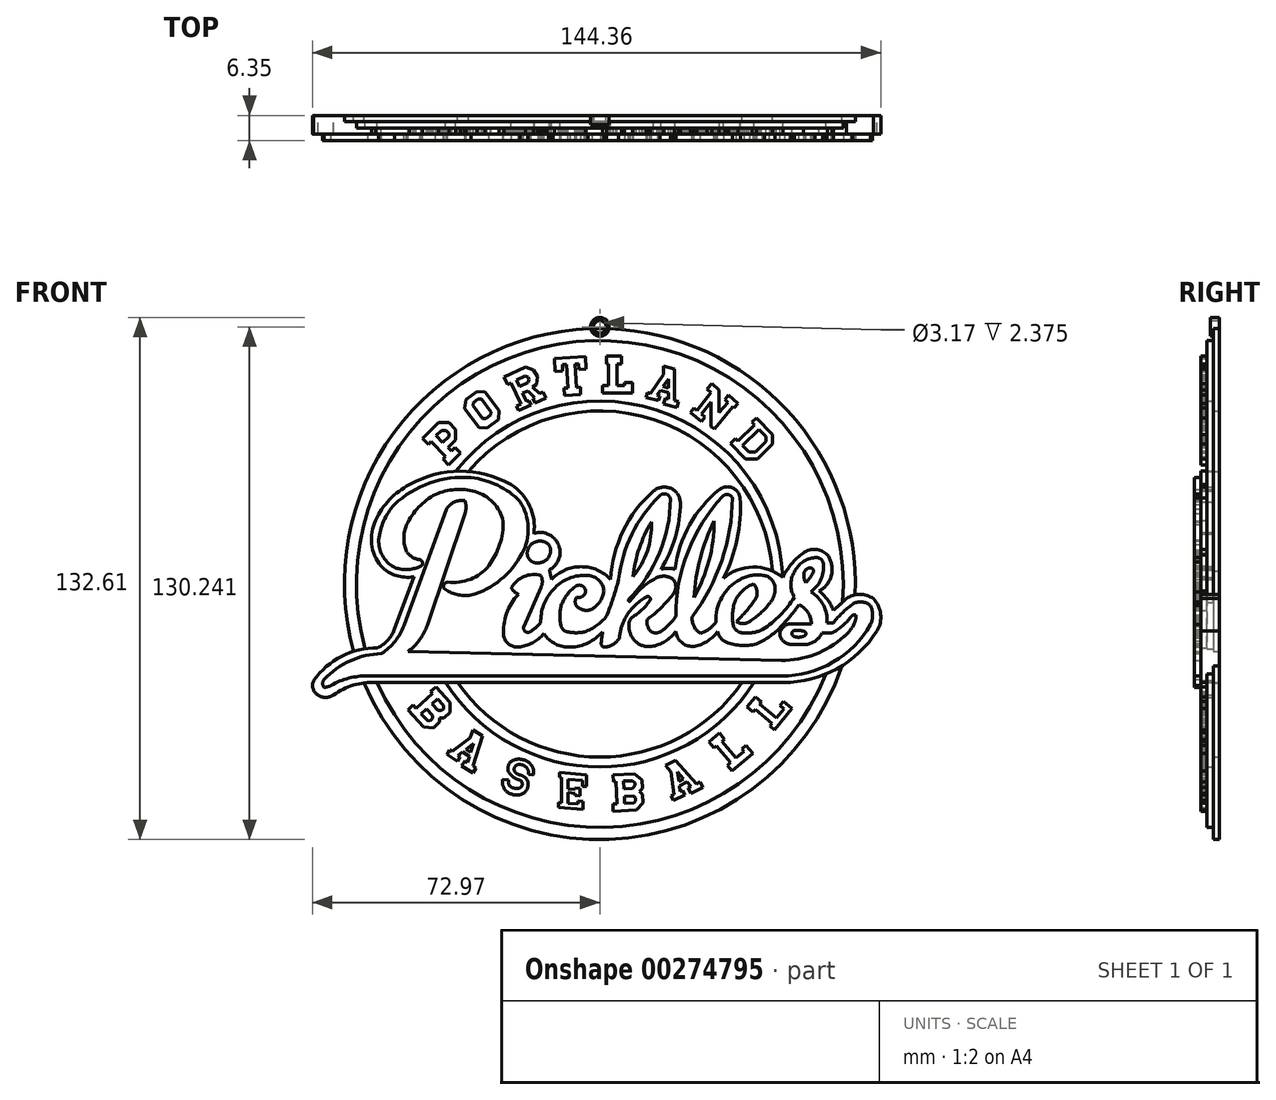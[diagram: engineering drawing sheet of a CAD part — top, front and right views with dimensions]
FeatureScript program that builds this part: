
annotation { "Feature Type Name" : "Feature", "Feature Type Description" : "" }
export const myFeature = defineFeature(function(context is Context, id is Id, definition is map)
    precondition{}
    {
        {
            var Q0;
            Q0=qCreatedBy(makeId("Front.planeOp"),FACE);
            var sketch = newSketch(context, id + "F0", { "sketchPlane" : qUnion([Q0])});
            skCircle(sketch, "E0", {"center": v(0, 0) * mm, "radius": 64.91 * mm});
            skCircle(sketch, "E1", {"center": v(0, 0) * mm, "radius": 43.97 * mm});
            skSolve(sketch);
        }
        {
            var Q0;
            Q0=makeQuery(id+"F0.imprint","IMPRINT",FACE,{"disambiguationData":[TD([[makeQuery(id+"F0.imprint","IMPRINT",EDGE,{"derivedFrom":sQuery(id+"F0.wireOp",EDGE,"E0")}),1.0]])]});
            extrude(context, id + "F1", {"entities" : qUnion([Q0]), "depth" : 1.59 * mm});
        }
        {
            var Q0;
            Q0=makeQuery(id+"F1.opExtrude","CAP_FACE",FACE,{"disambiguationData":[OSD([sQuery(id+"F0.wireOp",EDGE,"E0"),sQuery(id+"F0.wireOp",EDGE,"E1")])],"isStart":false});
            var sketch = newSketch(context, id + "F2", { "sketchPlane" : qUnion([Q0])});
            skCircle(sketch, "E2", {"center": v(0, 0) * mm, "radius": 61.84 * mm});
            skCircle(sketch, "E3", {"center": v(0, 0) * mm, "radius": 46.5 * mm});
            skSolve(sketch);
        }
        {
            var Q0;
            Q0=makeQuery(id+"F2.imprint","IMPRINT",FACE,{"disambiguationData":[TD([[makeQuery(id+"F2.imprint","IMPRINT",EDGE,{"derivedFrom":sQuery(id+"F2.wireOp",EDGE,"E2")}),1.0]])]});
            extrude(context, id + "F3", {"entities" : qUnion([Q0]), "operationType" : NewBodyOperationType.ADD, "depth" : 1.59 * mm});
        }
        {
            var Q0;
            Q0=makeQuery(id+"F3.opExtrude","CAP_FACE",FACE,{"disambiguationData":[OSD([sQuery(id+"F2.wireOp",EDGE,"E2"),sQuery(id+"F2.wireOp",EDGE,"E3")])],"isStart":false});
            var sketch = newSketch(context, id + "F4", { "sketchPlane" : qUnion([Q0])});
            skLineSegment(sketch, "E4", {"start": v(-45, 37.01) * mm, "end": v(-43.54, 35.5) * mm});
            skLineSegment(sketch, "E5", {"start": v(-43.54, 35.5) * mm, "end": v(-42.88, 36.15) * mm});
            skLineSegment(sketch, "E6", {"start": v(-42.88, 36.15) * mm, "end": v(-39.2, 32.36) * mm});
            skLineSegment(sketch, "E7", {"start": v(-39.2, 32.36) * mm, "end": v(-39.83, 31.75) * mm});
            skLineSegment(sketch, "E8", {"start": v(-39.83, 31.75) * mm, "end": v(-38.41, 30.3) * mm});
            skLineSegment(sketch, "E9", {"start": v(-38.41, 30.3) * mm, "end": v(-35.38, 33.24) * mm});
            skLineSegment(sketch, "E10", {"start": v(-35.38, 33.24) * mm, "end": v(-36.8, 34.7) * mm});
            skLineSegment(sketch, "E11", {"start": v(-36.8, 34.7) * mm, "end": v(-37.7, 33.84) * mm});
            skLineSegment(sketch, "E12", {"start": v(-37.7, 33.84) * mm, "end": v(-38.57, 34.73) * mm});
            skLineSegment(sketch, "E13", {"start": v(-38.57, 34.73) * mm, "end": v(-36.65, 36.6) * mm});
            skLineSegment(sketch, "E14", {"start": v(-36.65, 36.6) * mm, "end": v(-36.65, 39.24) * mm});
            skLineSegment(sketch, "E15", {"start": v(-36.65, 39.24) * mm, "end": v(-38.37, 41.02) * mm});
            skLineSegment(sketch, "E16", {"start": v(-45, 37.01) * mm, "end": v(-40.92, 40.98) * mm});
            skLineSegment(sketch, "E17", {"start": v(-40.92, 40.98) * mm, "end": v(-38.37, 41.02) * mm});
            skLineSegment(sketch, "E18", {"start": v(-41.62, 37.68) * mm, "end": v(-40.2, 39.06) * mm});
            skLineSegment(sketch, "E19", {"start": v(-40.2, 39.06) * mm, "end": v(-39.12, 39.06) * mm});
            skLineSegment(sketch, "E20", {"start": v(-39.12, 39.06) * mm, "end": v(-38.37, 38.29) * mm});
            skLineSegment(sketch, "E21", {"start": v(-38.37, 38.29) * mm, "end": v(-38.37, 37.5) * mm});
            skLineSegment(sketch, "E22", {"start": v(-41.62, 37.68) * mm, "end": v(-39.95, 35.96) * mm});
            skLineSegment(sketch, "E23", {"start": v(-38.37, 37.5) * mm, "end": v(-39.95, 35.96) * mm});
            skLineSegment(sketch, "E24", {"start": v(-33.96, 46.9) * mm, "end": v(-31.25, 48.95) * mm});
            skLineSegment(sketch, "E25", {"start": v(-31.25, 48.95) * mm, "end": v(-29.18, 48.82) * mm});
            skLineSegment(sketch, "E26", {"start": v(-29.18, 48.82) * mm, "end": v(-25.57, 44.04) * mm});
            skLineSegment(sketch, "E27", {"start": v(-25.57, 44.04) * mm, "end": v(-25.7, 41.85) * mm});
            skLineSegment(sketch, "E28", {"start": v(-25.7, 41.85) * mm, "end": v(-28.67, 39.6) * mm});
            skLineSegment(sketch, "E29", {"start": v(-28.67, 39.6) * mm, "end": v(-30.7, 39.74) * mm});
            skLineSegment(sketch, "E30", {"start": v(-30.7, 39.74) * mm, "end": v(-34.33, 44.53) * mm});
            skLineSegment(sketch, "E31", {"start": v(-34.33, 44.53) * mm, "end": v(-33.96, 46.9) * mm});
            skLineSegment(sketch, "E32", {"start": v(-32.06, 46.14) * mm, "end": v(-30.93, 47) * mm});
            skLineSegment(sketch, "E33", {"start": v(-30.07, 46.95) * mm, "end": v(-27.63, 43.73) * mm});
            skLineSegment(sketch, "E34", {"start": v(-27.8, 42.88) * mm, "end": v(-28.94, 42.02) * mm});
            skLineSegment(sketch, "E35", {"start": v(-29.8, 42.09) * mm, "end": v(-32.24, 45.3) * mm});
            skLineSegment(sketch, "E36", {"start": v(-24.28, 52.53) * mm, "end": v(-18.82, 55.07) * mm});
            skLineSegment(sketch, "E37", {"start": v(-18.82, 55.07) * mm, "end": v(-16.83, 54.38) * mm});
            skLineSegment(sketch, "E38", {"start": v(-16.83, 54.38) * mm, "end": v(-15.86, 52.67) * mm});
            skLineSegment(sketch, "E39", {"start": v(-15.86, 52.67) * mm, "end": v(-16.12, 50.74) * mm});
            skLineSegment(sketch, "E40", {"start": v(-16.12, 50.74) * mm, "end": v(-17.06, 50.05) * mm});
            skLineSegment(sketch, "E41", {"start": v(-17.06, 50.05) * mm, "end": v(-15.38, 48.37) * mm});
            skLineSegment(sketch, "E42", {"start": v(-15.38, 48.37) * mm, "end": v(-14.38, 48.84) * mm});
            skLineSegment(sketch, "E43", {"start": v(-14.38, 48.84) * mm, "end": v(-13.66, 47.27) * mm});
            skLineSegment(sketch, "E44", {"start": v(-13.66, 47.27) * mm, "end": v(-16.45, 45.97) * mm});
            skLineSegment(sketch, "E45", {"start": v(-16.45, 45.97) * mm, "end": v(-16.98, 47.12) * mm});
            skLineSegment(sketch, "E46", {"start": v(-16.98, 47.12) * mm, "end": v(-16.56, 47.32) * mm});
            skLineSegment(sketch, "E47", {"start": v(-16.56, 47.32) * mm, "end": v(-18.3, 49.06) * mm});
            skLineSegment(sketch, "E48", {"start": v(-18.3, 49.06) * mm, "end": v(-19.58, 48.47) * mm});
            skLineSegment(sketch, "E49", {"start": v(-19.58, 48.47) * mm, "end": v(-18.7, 46.55) * mm});
            skPoint(sketch, "E49.endSnap0", {"position": v(-16.72, 46.55) * mm});
            skLineSegment(sketch, "E50", {"start": v(-17.96, 46.67) * mm, "end": v(-18.6, 46.37) * mm});
            skLineSegment(sketch, "E51", {"start": v(-18.7, 46.55) * mm, "end": v(-18.6, 46.37) * mm});
            skLineSegment(sketch, "E52", {"start": v(-17.96, 46.67) * mm, "end": v(-17.42, 45.52) * mm});
            skLineSegment(sketch, "E53", {"start": v(-17.42, 45.52) * mm, "end": v(-20.63, 44.03) * mm});
            skPoint(sketch, "E54.orphan", {"position": v(-18.93, 46.22) * mm});
            skLineSegment(sketch, "E55", {"start": v(-20.63, 44.03) * mm, "end": v(-21.17, 45.18) * mm});
            skLineSegment(sketch, "E56", {"start": v(-20.07, 45.69) * mm, "end": v(-22.6, 51.12) * mm});
            skLineSegment(sketch, "E57", {"start": v(-22.6, 51.12) * mm, "end": v(-23.45, 50.73) * mm});
            skLineSegment(sketch, "E58.trimOffspring", {"start": v(-20.07, 45.69) * mm, "end": v(-21.17, 45.18) * mm});
            skLineSegment(sketch, "E59", {"start": v(-24.28, 52.53) * mm, "end": v(-23.45, 50.73) * mm});
            skLineSegment(sketch, "E60", {"start": v(-21.14, 51.8) * mm, "end": v(-19, 52.8) * mm});
            skLineSegment(sketch, "E61", {"start": v(-18.2, 52.53) * mm, "end": v(-17.94, 51.95) * mm});
            skLineSegment(sketch, "E62", {"start": v(-18.25, 51.17) * mm, "end": v(-20.38, 50.18) * mm});
            skPoint(sketch, "E63.trimOffspring.end.orphan", {"position": v(-22.6, 54.96) * mm});
            skPoint(sketch, "E64.orphan", {"position": v(-14.3, 54.99) * mm});
            skLineSegment(sketch, "E65", {"start": v(-20.38, 50.18) * mm, "end": v(-21.14, 51.8) * mm});
            skLineSegment(sketch, "E66", {"start": v(-19, 52.8) * mm, "end": v(-18.2, 52.53) * mm});
            skLineSegment(sketch, "E67", {"start": v(-18.25, 51.17) * mm, "end": v(-17.94, 51.95) * mm});
            skPoint(sketch, "E68.orphan", {"position": v(-17.7, 49.97) * mm});
            skPoint(sketch, "E69.orphan", {"position": v(-18.45, 53.06) * mm});
            skPoint(sketch, "E70.orphan", {"position": v(-17.7, 51.43) * mm});
            skLineSegment(sketch, "E71", {"start": v(-30.07, 46.95) * mm, "end": v(-30.93, 47) * mm});
            skPoint(sketch, "E72.trimOffspring.end.orphan", {"position": v(-29.43, 44.98) * mm});
            skPoint(sketch, "E73.orphan", {"position": v(-29.3, 46.9) * mm});
            skLineSegment(sketch, "E74", {"start": v(-32.24, 45.3) * mm, "end": v(-32.06, 46.14) * mm});
            skLineSegment(sketch, "E75", {"start": v(-28.94, 42.02) * mm, "end": v(-29.8, 42.09) * mm});
            skLineSegment(sketch, "E76", {"start": v(-27.8, 42.88) * mm, "end": v(-27.63, 43.73) * mm});
            skLineSegment(sketch, "E77", {"start": v(-4.17, 57.71) * mm, "end": v(-11.54, 57.23) * mm});
            skLineSegment(sketch, "E78", {"start": v(-11.54, 57.23) * mm, "end": v(-11.33, 54.04) * mm});
            skLineSegment(sketch, "E79", {"start": v(-9.42, 54.17) * mm, "end": v(-9.47, 54.9) * mm});
            skLineSegment(sketch, "E80", {"start": v(-8.4, 54.96) * mm, "end": v(-8.06, 49.81) * mm});
            skLineSegment(sketch, "E81", {"start": v(-8.06, 49.81) * mm, "end": v(-9.05, 49.75) * mm});
            skLineSegment(sketch, "E82", {"start": v(-9.05, 49.75) * mm, "end": v(-8.93, 47.87) * mm});
            skLineSegment(sketch, "E83", {"start": v(-8.93, 47.87) * mm, "end": v(-4.85, 48.14) * mm});
            skLineSegment(sketch, "E84", {"start": v(-6.32, 55.1) * mm, "end": v(-5.98, 49.97) * mm});
            skPoint(sketch, "E84.endSnap0", {"position": v(-5.64, 49.97) * mm});
            skLineSegment(sketch, "E85", {"start": v(-4.85, 48.14) * mm, "end": v(-4.97, 50.02) * mm});
            skLineSegment(sketch, "E86", {"start": v(-4.17, 57.71) * mm, "end": v(-3.7, 57.74) * mm});
            skLineSegment(sketch, "E87", {"start": v(-3.7, 57.74) * mm, "end": v(-3.5, 54.56) * mm});
            skLineSegment(sketch, "E88.trimOffspring", {"start": v(-5.26, 54.44) * mm, "end": v(-5.31, 55.17) * mm});
            skPoint(sketch, "E89.orphan", {"position": v(-3.22, 50.13) * mm});
            skLineSegment(sketch, "E90", {"start": v(-4.97, 50.02) * mm, "end": v(-5.98, 49.95) * mm});
            skLineSegment(sketch, "E91", {"start": v(-5.98, 49.97) * mm, "end": v(-5.98, 49.95) * mm});
            skLineSegment(sketch, "E92", {"start": v(-9.47, 54.9) * mm, "end": v(-9.52, 55.7) * mm});
            skLineSegment(sketch, "E93", {"start": v(-8.4, 54.96) * mm, "end": v(-8.46, 55.77) * mm});
            skLineSegment(sketch, "E94", {"start": v(-6.32, 55.1) * mm, "end": v(-6.37, 55.9) * mm});
            skLineSegment(sketch, "E95", {"start": v(-5.31, 55.17) * mm, "end": v(-5.36, 55.98) * mm});
            skLineSegment(sketch, "E96", {"start": v(-9.52, 55.7) * mm, "end": v(-8.46, 55.77) * mm});
            skLineSegment(sketch, "E97.trimOffspring", {"start": v(-6.37, 55.9) * mm, "end": v(-5.36, 55.98) * mm});
            skLineSegment(sketch, "E98", {"start": v(-5.26, 54.44) * mm, "end": v(-3.5, 54.56) * mm});
            skLineSegment(sketch, "E99", {"start": v(-9.42, 54.17) * mm, "end": v(-11.33, 54.04) * mm});
            skPoint(sketch, "E100.orphan", {"position": v(-5.22, 53.71) * mm});
            skLineSegment(sketch, "E101", {"start": v(1.68, 57.94) * mm, "end": v(5.56, 57.94) * mm});
            skLineSegment(sketch, "E102", {"start": v(5.56, 57.94) * mm, "end": v(5.56, 55.91) * mm});
            skLineSegment(sketch, "E103", {"start": v(5.56, 55.91) * mm, "end": v(4.33, 55.91) * mm});
            skLineSegment(sketch, "E104", {"start": v(4.33, 55.91) * mm, "end": v(4.33, 50.37) * mm});
            skLineSegment(sketch, "E105", {"start": v(4.33, 50.37) * mm, "end": v(6.25, 50.37) * mm});
            skLineSegment(sketch, "E106", {"start": v(6.25, 50.37) * mm, "end": v(6.25, 51.2) * mm});
            skLineSegment(sketch, "E107", {"start": v(6.25, 51.2) * mm, "end": v(8.32, 51.2) * mm});
            skLineSegment(sketch, "E108", {"start": v(8.32, 51.2) * mm, "end": v(8.32, 48.49) * mm});
            skLineSegment(sketch, "E109", {"start": v(8.32, 48.49) * mm, "end": v(0.63, 48.49) * mm});
            skLineSegment(sketch, "E110", {"start": v(0.63, 48.49) * mm, "end": v(0.63, 50.37) * mm});
            skLineSegment(sketch, "E111", {"start": v(0.63, 50.37) * mm, "end": v(2.18, 50.37) * mm});
            skLineSegment(sketch, "E112", {"start": v(2.18, 50.37) * mm, "end": v(2.18, 55.91) * mm});
            skLineSegment(sketch, "E113", {"start": v(2.18, 55.91) * mm, "end": v(1.68, 55.91) * mm});
            skLineSegment(sketch, "E114", {"start": v(1.68, 55.91) * mm, "end": v(1.68, 57.94) * mm});
            skPoint(sketch, "E115.endSnap0", {"position": v(16.46, 48.8) * mm});
            skLineSegment(sketch, "E116", {"start": v(16.22, 45.8) * mm, "end": v(19.55, 44.89) * mm});
            skLineSegment(sketch, "E117", {"start": v(19.95, 46.35) * mm, "end": v(19, 46.61) * mm});
            skLineSegment(sketch, "E118", {"start": v(19, 46.61) * mm, "end": v(19, 54.59) * mm});
            skLineSegment(sketch, "E119", {"start": v(16.14, 53.17) * mm, "end": v(13.1, 48.82) * mm});
            skLineSegment(sketch, "E120", {"start": v(17.44, 47.04) * mm, "end": v(16.62, 47.26) * mm});
            skLineSegment(sketch, "E121", {"start": v(16.22, 45.8) * mm, "end": v(16.62, 47.26) * mm});
            skLineSegment(sketch, "E122", {"start": v(11.77, 47.41) * mm, "end": v(14.88, 46.57) * mm});
            skLineSegment(sketch, "E123", {"start": v(14.88, 46.57) * mm, "end": v(15.22, 47.8) * mm});
            skLineSegment(sketch, "E124", {"start": v(15.22, 47.8) * mm, "end": v(14.57, 47.99) * mm});
            skLineSegment(sketch, "E125", {"start": v(13.1, 48.82) * mm, "end": v(12.85, 48.45) * mm});
            skLineSegment(sketch, "E126", {"start": v(14.57, 47.99) * mm, "end": v(15.2, 48.9) * mm});
            skLineSegment(sketch, "E127", {"start": v(17.44, 48.44) * mm, "end": v(17.44, 47.04) * mm});
            skLineSegment(sketch, "E128", {"start": v(15.51, 49.13) * mm, "end": v(17.44, 48.6) * mm});
            skLineSegment(sketch, "E129", {"start": v(17.44, 48.6) * mm, "end": v(17.44, 48.44) * mm});
            skLineSegment(sketch, "E130", {"start": v(15.2, 48.9) * mm, "end": v(15.4, 49.16) * mm});
            skLineSegment(sketch, "E131", {"start": v(15.51, 49.13) * mm, "end": v(15.4, 49.16) * mm});
            skLineSegment(sketch, "E132", {"start": v(19, 54.59) * mm, "end": v(16.18, 55.35) * mm});
            skLineSegment(sketch, "E133", {"start": v(16.18, 55.35) * mm, "end": v(16.14, 53.17) * mm});
            skLineSegment(sketch, "E134", {"start": v(16.07, 50.12) * mm, "end": v(17.4, 49.76) * mm});
            skLineSegment(sketch, "E135", {"start": v(17.4, 49.76) * mm, "end": v(17.4, 52.14) * mm});
            skLineSegment(sketch, "E136", {"start": v(17.4, 52.14) * mm, "end": v(16.07, 50.12) * mm});
            skLineSegment(sketch, "E137.trimOffspring", {"start": v(12.85, 48.45) * mm, "end": v(12.1, 48.66) * mm});
            skLineSegment(sketch, "E138", {"start": v(12.1, 48.66) * mm, "end": v(11.77, 47.41) * mm});
            skLineSegment(sketch, "E139", {"start": v(19.95, 46.35) * mm, "end": v(19.55, 44.89) * mm});
            skLineSegment(sketch, "E140", {"start": v(28.44, 50.95) * mm, "end": v(30.3, 49.32) * mm});
            skLineSegment(sketch, "E141", {"start": v(30.3, 49.32) * mm, "end": v(30.3, 43.62) * mm});
            skLineSegment(sketch, "E142", {"start": v(32.75, 47.97) * mm, "end": v(35.12, 45.9) * mm});
            skLineSegment(sketch, "E143", {"start": v(35.12, 45.9) * mm, "end": v(34.32, 44.97) * mm});
            skLineSegment(sketch, "E144", {"start": v(33.77, 45.07) * mm, "end": v(29.11, 39.33) * mm});
            skLineSegment(sketch, "E145", {"start": v(28.29, 40) * mm, "end": v(28.29, 46.3) * mm});
            skLineSegment(sketch, "E146", {"start": v(28.29, 46.3) * mm, "end": v(26.06, 43.55) * mm});
            skLineSegment(sketch, "E147", {"start": v(26.06, 43.55) * mm, "end": v(25.77, 43.2) * mm});
            skLineSegment(sketch, "E148", {"start": v(25.77, 43.2) * mm, "end": v(26.67, 42.46) * mm});
            skLineSegment(sketch, "E149", {"start": v(25.76, 41.33) * mm, "end": v(23.01, 43.56) * mm});
            skLineSegment(sketch, "E150", {"start": v(26.67, 42.46) * mm, "end": v(25.76, 41.33) * mm});
            skLineSegment(sketch, "E151", {"start": v(32.75, 47.97) * mm, "end": v(31.94, 47.04) * mm});
            skLineSegment(sketch, "E152", {"start": v(31.76, 46.83) * mm, "end": v(32.53, 46.16) * mm});
            skLineSegment(sketch, "E153", {"start": v(31.94, 47.04) * mm, "end": v(31.76, 46.83) * mm});
            skLineSegment(sketch, "E154", {"start": v(34.32, 44.97) * mm, "end": v(34.13, 44.76) * mm});
            skLineSegment(sketch, "E155", {"start": v(30.3, 43.62) * mm, "end": v(32.53, 46.16) * mm});
            skLineSegment(sketch, "E156.trimOffspring", {"start": v(33.77, 45.07) * mm, "end": v(34.13, 44.76) * mm});
            skLineSegment(sketch, "E157", {"start": v(28.44, 50.95) * mm, "end": v(27.27, 49.5) * mm});
            skLineSegment(sketch, "E158", {"start": v(24.62, 44.13) * mm, "end": v(23.93, 44.7) * mm});
            skLineSegment(sketch, "E159", {"start": v(23.01, 43.56) * mm, "end": v(23.93, 44.7) * mm});
            skLineSegment(sketch, "E160", {"start": v(24.62, 44.13) * mm, "end": v(27.98, 48.26) * mm});
            skLineSegment(sketch, "E161", {"start": v(27.98, 48.26) * mm, "end": v(28.3, 48.66) * mm});
            skLineSegment(sketch, "E162", {"start": v(28.3, 48.66) * mm, "end": v(27.27, 49.5) * mm});
            skPoint(sketch, "E163.orphan", {"position": v(27.81, 39.67) * mm});
            skLineSegment(sketch, "E164", {"start": v(28.29, 40) * mm, "end": v(29.11, 39.33) * mm});
            skPoint(sketch, "E165.orphan", {"position": v(28.29, 39.29) * mm});
            skPoint(sketch, "E166.orphan", {"position": v(29.17, 39.29) * mm});
            skPoint(sketch, "E167.orphan", {"position": v(28.76, 38.9) * mm});
            skLineSegment(sketch, "E168", {"start": v(39.8, 42.2) * mm, "end": v(43.91, 38) * mm});
            skPoint(sketch, "E168.startSnap0", {"position": v(31.44, 42.2) * mm});
            skLineSegment(sketch, "E169", {"start": v(43.91, 38) * mm, "end": v(43.92, 35.6) * mm});
            skLineSegment(sketch, "E170", {"start": v(43.92, 35.6) * mm, "end": v(40.1, 31.82) * mm});
            skLineSegment(sketch, "E171", {"start": v(40.1, 31.82) * mm, "end": v(36.96, 31.82) * mm});
            skLineSegment(sketch, "E172", {"start": v(36.96, 31.82) * mm, "end": v(33.16, 35.7) * mm});
            skLineSegment(sketch, "E173", {"start": v(39.8, 42.2) * mm, "end": v(38.67, 41.1) * mm});
            skLineSegment(sketch, "E174", {"start": v(38.67, 41.1) * mm, "end": v(39.3, 40.46) * mm});
            skLineSegment(sketch, "E175", {"start": v(39.3, 40.46) * mm, "end": v(35.08, 36.33) * mm});
            skLineSegment(sketch, "E176", {"start": v(35.08, 36.33) * mm, "end": v(34.45, 36.97) * mm});
            skLineSegment(sketch, "E177", {"start": v(40.48, 39.26) * mm, "end": v(42.25, 37.44) * mm});
            skLineSegment(sketch, "E178.trimOffspring", {"start": v(34.45, 36.97) * mm, "end": v(33.16, 35.7) * mm});
            skLineSegment(sketch, "E179", {"start": v(42.25, 37.44) * mm, "end": v(42.25, 36.2) * mm});
            skLineSegment(sketch, "E180", {"start": v(42.25, 36.2) * mm, "end": v(39.5, 33.5) * mm});
            skLineSegment(sketch, "E181", {"start": v(39.5, 33.5) * mm, "end": v(37.84, 33.5) * mm});
            skLineSegment(sketch, "E182", {"start": v(40.48, 39.26) * mm, "end": v(36.26, 35.13) * mm});
            skPoint(sketch, "E183.orphan", {"position": v(45.2, 34.43) * mm});
            skLineSegment(sketch, "E184", {"start": v(36.26, 35.13) * mm, "end": v(37.84, 33.5) * mm});
            skLineSegment(sketch, "E185", {"start": v(-48.78, -32.01) * mm, "end": v(-47.4, -30.75) * mm});
            skLineSegment(sketch, "E186", {"start": v(-47.4, -30.75) * mm, "end": v(-46.64, -31.58) * mm});
            skLineSegment(sketch, "E187", {"start": v(-46.64, -31.58) * mm, "end": v(-42.48, -27.78) * mm});
            skLineSegment(sketch, "E188", {"start": v(-42.48, -27.78) * mm, "end": v(-42.96, -27.26) * mm});
            skLineSegment(sketch, "E189", {"start": v(-42.96, -27.26) * mm, "end": v(-41.68, -26.1) * mm});
            skLineSegment(sketch, "E190", {"start": v(-41.68, -26.1) * mm, "end": v(-38, -30.12) * mm});
            skLineSegment(sketch, "E191", {"start": v(-38, -30.12) * mm, "end": v(-38, -32.6) * mm});
            skLineSegment(sketch, "E192", {"start": v(-38, -32.6) * mm, "end": v(-39.56, -34.03) * mm});
            skLineSegment(sketch, "E193", {"start": v(-39.56, -34.03) * mm, "end": v(-40.68, -34.03) * mm});
            skLineSegment(sketch, "E194", {"start": v(-40.68, -34.03) * mm, "end": v(-40.68, -35.05) * mm});
            skLineSegment(sketch, "E195", {"start": v(-40.68, -35.05) * mm, "end": v(-42.3, -36.53) * mm});
            skLineSegment(sketch, "E196", {"start": v(-48.78, -32.01) * mm, "end": v(-44.8, -36.37) * mm});
            skLineSegment(sketch, "E197", {"start": v(-44.8, -36.37) * mm, "end": v(-42.3, -36.53) * mm});
            skLineSegment(sketch, "E198", {"start": v(-45.36, -33) * mm, "end": v(-43.8, -34.7) * mm});
            skLineSegment(sketch, "E199", {"start": v(-43.8, -34.7) * mm, "end": v(-43.1, -34.74) * mm});
            skLineSegment(sketch, "E200", {"start": v(-43.1, -34.74) * mm, "end": v(-42.53, -34.21) * mm});
            skLineSegment(sketch, "E201", {"start": v(-42.53, -34.21) * mm, "end": v(-42.48, -33.45) * mm});
            skLineSegment(sketch, "E202", {"start": v(-42.48, -33.45) * mm, "end": v(-44.02, -31.77) * mm});
            skLineSegment(sketch, "E203", {"start": v(-44.02, -31.77) * mm, "end": v(-45.36, -33) * mm});
            skLineSegment(sketch, "E204", {"start": v(-41.2, -29.2) * mm, "end": v(-39.7, -30.83) * mm});
            skLineSegment(sketch, "E205", {"start": v(-42.64, -30.51) * mm, "end": v(-41.2, -29.2) * mm});
            skLineSegment(sketch, "E206", {"start": v(-40.19, -32.14) * mm, "end": v(-39.7, -31.7) * mm});
            skLineSegment(sketch, "E207", {"start": v(-39.7, -31.7) * mm, "end": v(-39.7, -30.83) * mm});
            skLineSegment(sketch, "E208", {"start": v(-42.64, -30.51) * mm, "end": v(-41.15, -32.14) * mm});
            skLineSegment(sketch, "E209", {"start": v(-41.15, -32.14) * mm, "end": v(-40.19, -32.14) * mm});
            skLineSegment(sketch, "E210", {"start": v(-35.14, -46.17) * mm, "end": v(-32.25, -48.06) * mm});
            skLineSegment(sketch, "E211", {"start": v(-31.42, -46.78) * mm, "end": v(-32.24, -46.25) * mm});
            skLineSegment(sketch, "E212", {"start": v(-32.24, -46.25) * mm, "end": v(-29.78, -38.66) * mm});
            skLineSegment(sketch, "E213", {"start": v(-32.94, -39.12) * mm, "end": v(-37.18, -42.32) * mm});
            skLineSegment(sketch, "E214", {"start": v(-33.6, -45.36) * mm, "end": v(-34.3, -44.9) * mm});
            skLineSegment(sketch, "E215", {"start": v(-35.14, -46.17) * mm, "end": v(-34.3, -44.9) * mm});
            skLineSegment(sketch, "E216", {"start": v(-38.87, -43.25) * mm, "end": v(-36.17, -45.01) * mm});
            skLineSegment(sketch, "E217", {"start": v(-36.17, -45.01) * mm, "end": v(-35.47, -43.94) * mm});
            skLineSegment(sketch, "E218", {"start": v(-35.47, -43.94) * mm, "end": v(-36.03, -43.57) * mm});
            skLineSegment(sketch, "E219", {"start": v(-37.18, -42.32) * mm, "end": v(-37.53, -42.6) * mm});
            skLineSegment(sketch, "E220", {"start": v(-36.03, -43.57) * mm, "end": v(-35.15, -42.9) * mm});
            skLineSegment(sketch, "E221", {"start": v(-33.17, -44.02) * mm, "end": v(-33.6, -45.36) * mm});
            skLineSegment(sketch, "E222", {"start": v(-34.79, -42.77) * mm, "end": v(-33.12, -43.87) * mm});
            skLineSegment(sketch, "E223", {"start": v(-35.15, -42.9) * mm, "end": v(-34.9, -42.7) * mm});
            skLineSegment(sketch, "E224", {"start": v(-34.79, -42.77) * mm, "end": v(-34.9, -42.7) * mm});
            skLineSegment(sketch, "E225", {"start": v(-29.78, -38.66) * mm, "end": v(-32.23, -37.06) * mm});
            skLineSegment(sketch, "E226", {"start": v(-32.23, -37.06) * mm, "end": v(-32.94, -39.12) * mm});
            skLineSegment(sketch, "E227", {"start": v(-33.95, -42) * mm, "end": v(-32.8, -42.76) * mm});
            skLineSegment(sketch, "E228", {"start": v(-32.8, -42.76) * mm, "end": v(-32.05, -40.5) * mm});
            skLineSegment(sketch, "E229", {"start": v(-32.05, -40.5) * mm, "end": v(-33.95, -42) * mm});
            skLineSegment(sketch, "E230.trimOffspring", {"start": v(-37.53, -42.6) * mm, "end": v(-38.17, -42.17) * mm});
            skLineSegment(sketch, "E231", {"start": v(-38.17, -42.17) * mm, "end": v(-38.87, -43.25) * mm});
            skLineSegment(sketch, "E232", {"start": v(-31.42, -46.78) * mm, "end": v(-32.25, -48.06) * mm});
            skLineSegment(sketch, "E233", {"start": v(23.1, -53.2) * mm, "end": v(26.17, -51.65) * mm});
            skLineSegment(sketch, "E234", {"start": v(25.48, -50.3) * mm, "end": v(24.6, -50.73) * mm});
            skLineSegment(sketch, "E235", {"start": v(24.6, -50.73) * mm, "end": v(19.26, -44.82) * mm});
            skLineSegment(sketch, "E236", {"start": v(18.08, -47.79) * mm, "end": v(18.75, -53.06) * mm});
            skLineSegment(sketch, "E237", {"start": v(23.16, -51.47) * mm, "end": v(22.4, -51.85) * mm});
            skLineSegment(sketch, "E238", {"start": v(23.1, -53.2) * mm, "end": v(22.4, -51.85) * mm});
            skLineSegment(sketch, "E239", {"start": v(18.7, -55) * mm, "end": v(21.58, -53.53) * mm});
            skLineSegment(sketch, "E240", {"start": v(21.58, -53.53) * mm, "end": v(21, -52.38) * mm});
            skLineSegment(sketch, "E241", {"start": v(21, -52.38) * mm, "end": v(20.4, -52.69) * mm});
            skLineSegment(sketch, "E242", {"start": v(18.75, -53.06) * mm, "end": v(18.8, -53.5) * mm});
            skLineSegment(sketch, "E243", {"start": v(20.4, -52.69) * mm, "end": v(20.26, -51.6) * mm});
            skLineSegment(sketch, "E244", {"start": v(22.22, -50.43) * mm, "end": v(23.16, -51.47) * mm});
            skLineSegment(sketch, "E245", {"start": v(20.33, -51.21) * mm, "end": v(22.1, -50.3) * mm});
            skLineSegment(sketch, "E246", {"start": v(22.1, -50.3) * mm, "end": v(22.22, -50.43) * mm});
            skLineSegment(sketch, "E247", {"start": v(20.26, -51.6) * mm, "end": v(20.22, -51.27) * mm});
            skLineSegment(sketch, "E248", {"start": v(20.33, -51.21) * mm, "end": v(20.22, -51.27) * mm});
            skLineSegment(sketch, "E249", {"start": v(19.26, -44.82) * mm, "end": v(16.65, -46.14) * mm});
            skLineSegment(sketch, "E250", {"start": v(16.65, -46.14) * mm, "end": v(18.08, -47.79) * mm});
            skLineSegment(sketch, "E251", {"start": v(20.08, -50.1) * mm, "end": v(21.31, -49.47) * mm});
            skLineSegment(sketch, "E252", {"start": v(21.31, -49.47) * mm, "end": v(19.71, -47.7) * mm});
            skLineSegment(sketch, "E253", {"start": v(19.71, -47.7) * mm, "end": v(20.08, -50.1) * mm});
            skLineSegment(sketch, "E254.trimOffspring", {"start": v(18.8, -53.5) * mm, "end": v(18.12, -53.85) * mm});
            skLineSegment(sketch, "E255", {"start": v(18.12, -53.85) * mm, "end": v(18.7, -55) * mm});
            skLineSegment(sketch, "E256", {"start": v(25.48, -50.3) * mm, "end": v(26.17, -51.65) * mm});
            skLineSegment(sketch, "E257.0", {"start": v(22.22, -50.43) * mm, "end": v(22.1, -50.3) * mm, "construction": true});
            skLineSegment(sketch, "E258", {"start": v(27.73, -40.12) * mm, "end": v(30.38, -37.9) * mm});
            skLineSegment(sketch, "E259", {"start": v(31.68, -39.45) * mm, "end": v(31.07, -39.96) * mm});
            skLineSegment(sketch, "E260", {"start": v(31.07, -39.96) * mm, "end": v(34.63, -44.21) * mm});
            skLineSegment(sketch, "E261", {"start": v(34.63, -44.21) * mm, "end": v(36.1, -42.98) * mm});
            skLineSegment(sketch, "E262", {"start": v(36.13, -41.85) * mm, "end": v(37.14, -41) * mm});
            skLineSegment(sketch, "E263", {"start": v(37.14, -41) * mm, "end": v(38.9, -43.09) * mm});
            skLineSegment(sketch, "E264", {"start": v(38.9, -43.09) * mm, "end": v(33.6, -47.53) * mm});
            skLineSegment(sketch, "E265", {"start": v(32.38, -46.1) * mm, "end": v(32.98, -45.6) * mm});
            skLineSegment(sketch, "E266", {"start": v(29.41, -41.35) * mm, "end": v(29.03, -41.67) * mm});
            skLineSegment(sketch, "E267", {"start": v(29.03, -41.67) * mm, "end": v(27.73, -40.12) * mm});
            skLineSegment(sketch, "E268.0", {"start": v(29.41, -41.35) * mm, "end": v(31.07, -39.96) * mm, "construction": true});
            skLineSegment(sketch, "E269.0", {"start": v(32.38, -46.1) * mm, "end": v(36.1, -42.98) * mm, "construction": true});
            skLineSegment(sketch, "E270.0", {"start": v(29.03, -41.67) * mm, "end": v(27.73, -40.12) * mm, "construction": true});
            skLineSegment(sketch, "E271", {"start": v(37.35, -31.25) * mm, "end": v(39.53, -28.66) * mm});
            skLineSegment(sketch, "E272", {"start": v(41.08, -29.96) * mm, "end": v(40.61, -30.52) * mm});
            skLineSegment(sketch, "E273", {"start": v(40.61, -30.52) * mm, "end": v(44.86, -34.08) * mm});
            skLineSegment(sketch, "E274", {"start": v(44.86, -34.08) * mm, "end": v(46.1, -32.61) * mm});
            skLineSegment(sketch, "E275", {"start": v(43.19, -36.08) * mm, "end": v(43.47, -35.73) * mm});
            skLineSegment(sketch, "E276", {"start": v(39.23, -32.17) * mm, "end": v(38.9, -32.55) * mm});
            skLineSegment(sketch, "E277", {"start": v(38.9, -32.55) * mm, "end": v(37.35, -31.25) * mm});
            skLineSegment(sketch, "E278.0", {"start": v(39.23, -32.17) * mm, "end": v(40.61, -30.52) * mm, "construction": true});
            skLineSegment(sketch, "E279.0", {"start": v(43.47, -35.73) * mm, "end": v(46.1, -32.61) * mm, "construction": true});
            skLineSegment(sketch, "E280.0", {"start": v(38.9, -32.55) * mm, "end": v(37.35, -31.25) * mm, "construction": true});
            skLineSegment(sketch, "E281", {"start": v(46.1, -32.61) * mm, "end": v(46.77, -31.8) * mm});
            skLineSegment(sketch, "E282", {"start": v(46.77, -31.8) * mm, "end": v(45.7, -30.9) * mm});
            skLineSegment(sketch, "E283", {"start": v(45.7, -30.9) * mm, "end": v(46.65, -29.79) * mm});
            skLineSegment(sketch, "E284", {"start": v(46.65, -29.79) * mm, "end": v(48.85, -31.63) * mm});
            skLineSegment(sketch, "E285", {"start": v(48.85, -31.63) * mm, "end": v(44.32, -37.03) * mm});
            skLineSegment(sketch, "E286", {"start": v(44.32, -37.03) * mm, "end": v(43.19, -36.08) * mm});
            skLineSegment(sketch, "E287", {"start": v(41.08, -29.96) * mm, "end": v(39.53, -28.66) * mm});
            skLineSegment(sketch, "E288", {"start": v(43.47, -35.73) * mm, "end": v(43.76, -35.4) * mm});
            skLineSegment(sketch, "E289", {"start": v(43.76, -35.4) * mm, "end": v(39.51, -31.83) * mm});
            skLineSegment(sketch, "E290", {"start": v(39.51, -31.83) * mm, "end": v(39.23, -32.17) * mm});
            skLineSegment(sketch, "E291", {"start": v(30.38, -37.9) * mm, "end": v(31.68, -39.45) * mm});
            skLineSegment(sketch, "E292", {"start": v(32.38, -46.1) * mm, "end": v(33.6, -47.53) * mm});
            skPoint(sketch, "E293.orphan", {"position": v(31.79, -46.6) * mm});
            skLineSegment(sketch, "E294", {"start": v(36.1, -42.98) * mm, "end": v(36.67, -42.5) * mm});
            skLineSegment(sketch, "E295", {"start": v(36.67, -42.5) * mm, "end": v(36.13, -41.85) * mm});
            skLineSegment(sketch, "E296", {"start": v(29.41, -41.35) * mm, "end": v(29.68, -41.12) * mm});
            skLineSegment(sketch, "E297", {"start": v(29.68, -41.12) * mm, "end": v(33.24, -45.37) * mm});
            skLineSegment(sketch, "E298", {"start": v(33.24, -45.37) * mm, "end": v(32.98, -45.6) * mm});
            skLineSegment(sketch, "E299", {"start": v(3.4, -57.75) * mm, "end": v(3.3, -55.88) * mm});
            skLineSegment(sketch, "E300", {"start": v(3.3, -55.88) * mm, "end": v(4.42, -55.82) * mm});
            skLineSegment(sketch, "E301", {"start": v(4.42, -55.82) * mm, "end": v(4.12, -50.2) * mm});
            skLineSegment(sketch, "E302", {"start": v(4.12, -50.2) * mm, "end": v(3.42, -50.23) * mm});
            skLineSegment(sketch, "E303", {"start": v(3.42, -50.23) * mm, "end": v(3.32, -48.5) * mm});
            skLineSegment(sketch, "E304", {"start": v(3.32, -48.5) * mm, "end": v(8.77, -48.2) * mm});
            skLineSegment(sketch, "E305", {"start": v(8.77, -48.2) * mm, "end": v(10.69, -49.78) * mm});
            skLineSegment(sketch, "E306", {"start": v(10.69, -49.78) * mm, "end": v(10.8, -51.89) * mm});
            skLineSegment(sketch, "E307", {"start": v(10.8, -51.89) * mm, "end": v(10.09, -52.76) * mm});
            skLineSegment(sketch, "E308", {"start": v(10.09, -52.76) * mm, "end": v(10.88, -53.4) * mm});
            skLineSegment(sketch, "E309", {"start": v(10.88, -53.4) * mm, "end": v(11, -55.59) * mm});
            skLineSegment(sketch, "E310", {"start": v(3.4, -57.75) * mm, "end": v(9.3, -57.43) * mm});
            skLineSegment(sketch, "E311", {"start": v(9.3, -57.43) * mm, "end": v(11, -55.59) * mm});
            skLineSegment(sketch, "E312", {"start": v(6.33, -55.72) * mm, "end": v(8.63, -55.6) * mm});
            skLineSegment(sketch, "E313", {"start": v(8.63, -55.6) * mm, "end": v(9.1, -55.08) * mm});
            skLineSegment(sketch, "E314", {"start": v(9.1, -55.08) * mm, "end": v(9.06, -54.3) * mm});
            skLineSegment(sketch, "E315", {"start": v(9.06, -54.3) * mm, "end": v(8.5, -53.78) * mm});
            skLineSegment(sketch, "E316", {"start": v(8.5, -53.78) * mm, "end": v(6.23, -53.9) * mm});
            skLineSegment(sketch, "E317", {"start": v(6.23, -53.9) * mm, "end": v(6.33, -55.72) * mm});
            skLineSegment(sketch, "E318", {"start": v(6.03, -50.1) * mm, "end": v(8.24, -49.97) * mm});
            skLineSegment(sketch, "E319", {"start": v(6.13, -52.04) * mm, "end": v(6.03, -50.1) * mm});
            skLineSegment(sketch, "E320", {"start": v(8.95, -51.18) * mm, "end": v(8.9, -50.52) * mm});
            skLineSegment(sketch, "E321", {"start": v(8.9, -50.52) * mm, "end": v(8.24, -49.97) * mm});
            skLineSegment(sketch, "E322", {"start": v(6.13, -52.04) * mm, "end": v(8.33, -51.93) * mm});
            skLineSegment(sketch, "E323", {"start": v(8.33, -51.93) * mm, "end": v(8.95, -51.18) * mm});
            skArc(sketch, "E324", {"start": v(-16.94, -48.55) * mm, "mid": v(-16.88, -47.1) * mm, "end": v(-17.55, -45.8) * mm});
            skArc(sketch, "E325", {"start": v(-17.55, -45.8) * mm, "mid": v(-19.78, -44.58) * mm, "end": v(-22.3, -44.9) * mm});
            skArc(sketch, "E326", {"start": v(-22.3, -44.9) * mm, "mid": v(-23.3, -46.38) * mm, "end": v(-22.97, -48.14) * mm});
            skArc(sketch, "E327", {"start": v(-22.97, -48.14) * mm, "mid": v(-21.94, -49.12) * mm, "end": v(-20.65, -49.73) * mm});
            skArc(sketch, "E328", {"start": v(-20.5, -51.9) * mm, "mid": v(-19.7, -50.76) * mm, "end": v(-20.65, -49.73) * mm});
            skArc(sketch, "E329", {"start": v(-22.97, -51.25) * mm, "mid": v(-21.81, -51.87) * mm, "end": v(-20.5, -51.9) * mm});
            skArc(sketch, "E330", {"start": v(-23.18, -49.73) * mm, "mid": v(-23.2, -50.5) * mm, "end": v(-22.97, -51.25) * mm});
            skLineSegment(sketch, "E331", {"start": v(-23.18, -49.73) * mm, "end": v(-24.66, -49.58) * mm});
            skArc(sketch, "E332", {"start": v(-24.66, -49.58) * mm, "mid": v(-24.63, -51.23) * mm, "end": v(-23.78, -52.64) * mm});
            skArc(sketch, "E333", {"start": v(-23.78, -52.64) * mm, "mid": v(-21.57, -53.59) * mm, "end": v(-19.22, -53.11) * mm});
            skArc(sketch, "E334", {"start": v(-19.22, -53.11) * mm, "mid": v(-18.26, -51.47) * mm, "end": v(-18.55, -49.58) * mm});
            skLineSegment(sketch, "E335", {"start": v(-16.94, -48.55) * mm, "end": v(-18.07, -48.43) * mm});
            skArc(sketch, "E336", {"start": v(-18.07, -48.43) * mm, "mid": v(-18.85, -46.42) * mm, "end": v(-20.94, -45.92) * mm});
            skArc(sketch, "E337", {"start": v(-20.94, -45.92) * mm, "mid": v(-21.7, -46.72) * mm, "end": v(-21.57, -47.8) * mm});
            skArc(sketch, "E338", {"start": v(-18.55, -49.58) * mm, "mid": v(-19.35, -48.92) * mm, "end": v(-20.3, -48.52) * mm});
            skArc(sketch, "E339", {"start": v(-21.57, -47.8) * mm, "mid": v(-21, -48.26) * mm, "end": v(-20.3, -48.52) * mm});
            skLineSegment(sketch, "E340", {"start": v(-10.13, -47.85) * mm, "end": v(-3.58, -48.5) * mm});
            skLineSegment(sketch, "E341", {"start": v(-3.58, -48.5) * mm, "end": v(-3.32, -48.52) * mm});
            skLineSegment(sketch, "E342", {"start": v(-3.32, -48.52) * mm, "end": v(-3.32, -51.38) * mm});
            skLineSegment(sketch, "E343", {"start": v(-3.32, -51.38) * mm, "end": v(-4.47, -51.38) * mm});
            skLineSegment(sketch, "E344", {"start": v(-4.47, -51.38) * mm, "end": v(-4.47, -49.95) * mm});
            skLineSegment(sketch, "E345", {"start": v(-4.47, -49.95) * mm, "end": v(-8.08, -49.6) * mm});
            skLineSegment(sketch, "E346", {"start": v(-8.08, -49.6) * mm, "end": v(-8.08, -52.02) * mm});
            skLineSegment(sketch, "E347", {"start": v(-8.08, -52.02) * mm, "end": v(-6.3, -52.2) * mm});
            skLineSegment(sketch, "E348", {"start": v(-6.3, -52.2) * mm, "end": v(-6.3, -51.8) * mm});
            skLineSegment(sketch, "E349", {"start": v(-6.3, -51.8) * mm, "end": v(-5.03, -51.93) * mm});
            skLineSegment(sketch, "E350", {"start": v(-5.03, -51.93) * mm, "end": v(-5.03, -53.86) * mm});
            skLineSegment(sketch, "E351", {"start": v(-5.03, -53.86) * mm, "end": v(-6.3, -53.73) * mm});
            skLineSegment(sketch, "E352", {"start": v(-6.3, -53.73) * mm, "end": v(-6.3, -53.17) * mm});
            skLineSegment(sketch, "E353", {"start": v(-6.3, -53.17) * mm, "end": v(-8.08, -53) * mm});
            skLineSegment(sketch, "E354", {"start": v(-8.08, -53) * mm, "end": v(-8.08, -55.7) * mm});
            skLineSegment(sketch, "E355", {"start": v(-5.5, -55.86) * mm, "end": v(-5.49, -55.1) * mm});
            skLineSegment(sketch, "E356", {"start": v(-5.49, -55.1) * mm, "end": v(-4.29, -55.22) * mm});
            skLineSegment(sketch, "E357", {"start": v(-4.29, -55.22) * mm, "end": v(-4.29, -57.23) * mm});
            skLineSegment(sketch, "E358", {"start": v(-4.29, -57.23) * mm, "end": v(-10.56, -56.82) * mm});
            skLineSegment(sketch, "E359", {"start": v(-9.73, -55.58) * mm, "end": v(-9.73, -49.18) * mm});
            skLineSegment(sketch, "E360", {"start": v(-9.73, -49.18) * mm, "end": v(-10.2, -49.13) * mm});
            skLineSegment(sketch, "E361", {"start": v(-10.2, -49.13) * mm, "end": v(-10.2, -47.85) * mm});
            skLineSegment(sketch, "E362", {"start": v(-10.13, -47.85) * mm, "end": v(-10.2, -47.85) * mm});
            skLineSegment(sketch, "E363", {"start": v(-10.56, -55.53) * mm, "end": v(-9.73, -55.58) * mm});
            skPoint(sketch, "E364.orphan", {"position": v(-9.73, -55.78) * mm});
            skPoint(sketch, "E365.orphan", {"position": v(-8.08, -55.89) * mm});
            skLineSegment(sketch, "E366.trimOffspring", {"start": v(-8.08, -55.7) * mm, "end": v(-5.5, -55.86) * mm});
            skLineSegment(sketch, "E367", {"start": v(-10.56, -55.53) * mm, "end": v(-10.56, -56.82) * mm});
            skPoint(sketch, "E368.end.orphan", {"position": v(-11.38, -55.67) * mm});
            skPoint(sketch, "E368.start.orphan", {"position": v(-11.38, -55.48) * mm});
            skLineSegment(sketch, "E369", {"start": v(-33.17, -44.02) * mm, "end": v(-33.12, -43.87) * mm});
            skSolve(sketch);
        }
        {
            var Q0;
            Q0=makeQuery(id+"F4.imprint","IMPRINT",FACE,{"disambiguationData":[TD([[makeQuery(id+"F4.imprint","IMPRINT",EDGE,{"derivedFrom":sQuery(id+"F4.wireOp",EDGE,"E4")}),1.0]])]});
            var Q1;
            Q1=makeQuery(id+"F4.imprint","IMPRINT",FACE,{"disambiguationData":[TD([[makeQuery(id+"F4.imprint","IMPRINT",EDGE,{"derivedFrom":sQuery(id+"F4.wireOp",EDGE,"E24")}),-1.0]])]});
            var Q2;
            Q2=makeQuery(id+"F4.imprint","IMPRINT",FACE,{"disambiguationData":[TD([[makeQuery(id+"F4.imprint","IMPRINT",EDGE,{"derivedFrom":sQuery(id+"F4.wireOp",EDGE,"E36")}),-1.0]])]});
            var Q3;
            Q3=makeQuery(id+"F4.imprint","IMPRINT",FACE,{"disambiguationData":[TD([[makeQuery(id+"F4.imprint","IMPRINT",EDGE,{"derivedFrom":sQuery(id+"F4.wireOp",EDGE,"E77")}),1.0]])]});
            var Q4;
            Q4=makeQuery(id+"F4.imprint","IMPRINT",FACE,{"disambiguationData":[TD([[makeQuery(id+"F4.imprint","IMPRINT",EDGE,{"derivedFrom":sQuery(id+"F4.wireOp",EDGE,"E101")}),-1.0]])]});
            var Q5;
            Q5=makeQuery(id+"F4.imprint","IMPRINT",FACE,{"disambiguationData":[TD([[makeQuery(id+"F4.imprint","IMPRINT",EDGE,{"derivedFrom":sQuery(id+"F4.wireOp",EDGE,"E116")}),1.0]])]});
            var Q6;
            Q6=makeQuery(id+"F4.imprint","IMPRINT",FACE,{"disambiguationData":[TD([[makeQuery(id+"F4.imprint","IMPRINT",EDGE,{"derivedFrom":sQuery(id+"F4.wireOp",EDGE,"E140")}),-1.0]])]});
            var Q7;
            Q7=makeQuery(id+"F4.imprint","IMPRINT",FACE,{"disambiguationData":[TD([[makeQuery(id+"F4.imprint","IMPRINT",EDGE,{"derivedFrom":sQuery(id+"F4.wireOp",EDGE,"E168")}),-1.0]])]});
            var Q8;
            Q8=makeQuery(id+"F4.imprint","IMPRINT",FACE,{"disambiguationData":[TD([[makeQuery(id+"F4.imprint","IMPRINT",EDGE,{"derivedFrom":sQuery(id+"F4.wireOp",EDGE,"E185")}),-1.0]])]});
            var Q9;
            Q9=makeQuery(id+"F4.imprint","IMPRINT",FACE,{"disambiguationData":[TD([[makeQuery(id+"F4.imprint","IMPRINT",EDGE,{"derivedFrom":sQuery(id+"F4.wireOp",EDGE,"E210")}),1.0]])]});
            var Q10;
            Q10=makeQuery(id+"F4.imprint","IMPRINT",FACE,{"disambiguationData":[TD([[makeQuery(id+"F4.imprint","IMPRINT",EDGE,{"derivedFrom":sQuery(id+"F4.wireOp",EDGE,"E324")}),1.0]])]});
            var Q11;
            Q11=makeQuery(id+"F4.imprint","IMPRINT",FACE,{"disambiguationData":[TD([[makeQuery(id+"F4.imprint","IMPRINT",EDGE,{"derivedFrom":sQuery(id+"F4.wireOp",EDGE,"E340")}),-1.0]])]});
            var Q12;
            Q12=makeQuery(id+"F4.imprint","IMPRINT",FACE,{"disambiguationData":[TD([[makeQuery(id+"F4.imprint","IMPRINT",EDGE,{"derivedFrom":sQuery(id+"F4.wireOp",EDGE,"E299")}),-1.0]])]});
            var Q13;
            Q13=makeQuery(id+"F4.imprint","IMPRINT",FACE,{"disambiguationData":[TD([[makeQuery(id+"F4.imprint","IMPRINT",EDGE,{"derivedFrom":sQuery(id+"F4.wireOp",EDGE,"E233")}),1.0]])]});
            var Q14;
            Q14=makeQuery(id+"F4.imprint","IMPRINT",FACE,{"disambiguationData":[TD([[makeQuery(id+"F4.imprint","IMPRINT",EDGE,{"derivedFrom":sQuery(id+"F4.wireOp",EDGE,"E258")}),-1.0]])]});
            var Q15;
            Q15=makeQuery(id+"F4.imprint","IMPRINT",FACE,{"disambiguationData":[TD([[makeQuery(id+"F4.imprint","IMPRINT",EDGE,{"derivedFrom":sQuery(id+"F4.wireOp",EDGE,"E271")}),-1.0]])]});
            extrude(context, id + "F5", {"entities" : qUnion([Q0, Q1, Q2, Q3, Q4, Q5, Q6, Q7, Q8, Q9, Q10, Q11, Q12, Q13, Q14, Q15]), "operationType" : NewBodyOperationType.ADD, "depth" : 1.59 * mm});
        }
        {
            var Q0;
            {var subQ0=sQuery(id+"F2.wireOp",EDGE,"E2");var subQ1=sQuery(id+"F2.wireOp",EDGE,"E3");Q0=makeQuery(id+"F5.boolean.opBoolean","SPLIT",FACE,{"disambiguationData":[TD([makeQuery(id+"F3.opExtrude","SWEPT_FACE",FACE,{"disambiguationData":[OSD([subQ0])]})])],"derivedFrom":makeQuery(id+"F3.opExtrude","CAP_FACE",FACE,{"disambiguationData":[OSD([subQ0,subQ1])],"isStart":false})});}
            var sketch = newSketch(context, id + "F6", { "sketchPlane" : qUnion([Q0])});
            skArc(sketch, "E370", {"start": v(-56.46, -16.23) * mm, "mid": v(-65.6, -18.37) * mm, "end": v(-72.68, -24.54) * mm});
            skArc(sketch, "E371", {"start": v(-72.68, -24.54) * mm, "mid": v(-72.86, -26.57) * mm, "end": v(-71.65, -28.2) * mm});
            skArc(sketch, "E372", {"start": v(-71.65, -28.2) * mm, "mid": v(-69.64, -28.8) * mm, "end": v(-67.64, -28.2) * mm});
            skArc(sketch, "E373", {"start": v(-57, -25.04) * mm, "mid": v(-62.6, -25.7) * mm, "end": v(-67.64, -28.2) * mm});
            skLineSegment(sketch, "E374", {"start": v(-57, -25.04) * mm, "end": v(46.62, -25.04) * mm});
            skArc(sketch, "E375", {"start": v(46.62, -25.04) * mm, "mid": v(60.21, -21.54) * mm, "end": v(70.42, -11.9) * mm});
            skArc(sketch, "E376", {"start": v(70.42, -11.9) * mm, "mid": v(71.35, -7.65) * mm, "end": v(69.48, -3.73) * mm});
            skArc(sketch, "E377", {"start": v(69.48, -3.73) * mm, "mid": v(66.06, -2.64) * mm, "end": v(62.65, -3.73) * mm});
            skArc(sketch, "E378", {"start": v(59.32, -6.68) * mm, "mid": v(61, -5.22) * mm, "end": v(62.65, -3.73) * mm});
            skArc(sketch, "E379", {"start": v(59.32, -6.68) * mm, "mid": v(57.85, -3.98) * mm, "end": v(55.7, -1.8) * mm});
            skArc(sketch, "E380", {"start": v(55.7, -1.8) * mm, "mid": v(58.85, 2.3) * mm, "end": v(57.85, 7.37) * mm});
            skArc(sketch, "E381", {"start": v(57.85, 7.37) * mm, "mid": v(54.86, 8.77) * mm, "end": v(51.68, 7.86) * mm});
            skArc(sketch, "E382", {"start": v(51.68, 7.86) * mm, "mid": v(48.68, 5.06) * mm, "end": v(46.48, 1.6) * mm});
            skArc(sketch, "E383", {"start": v(46.48, 1.6) * mm, "mid": v(38.88, 4.3) * mm, "end": v(31.37, 1.38) * mm});
            skArc(sketch, "E384", {"start": v(31.37, 1.38) * mm, "mid": v(34.88, 11.36) * mm, "end": v(35.63, 21.91) * mm});
            skArc(sketch, "E385", {"start": v(35.63, 21.91) * mm, "mid": v(33.65, 24.47) * mm, "end": v(30.45, 24.03) * mm});
            skArc(sketch, "E386", {"start": v(30.45, 24.03) * mm, "mid": v(22.8, 15) * mm, "end": v(19.12, 3.75) * mm});
            skArc(sketch, "E387", {"start": v(19.12, 3.75) * mm, "mid": v(17.3, 3.99) * mm, "end": v(15.48, 3.75) * mm});
            skArc(sketch, "E388", {"start": v(15.48, 3.75) * mm, "mid": v(19.21, 11.92) * mm, "end": v(20.45, 20.8) * mm});
            skArc(sketch, "E389", {"start": v(20.45, 20.8) * mm, "mid": v(17.9, 24.34) * mm, "end": v(13.63, 23.58) * mm});
            skArc(sketch, "E390", {"start": v(13.63, 23.58) * mm, "mid": v(5.93, 13.5) * mm, "end": v(2.76, 1.21) * mm});
            skArc(sketch, "E391", {"start": v(2.76, 1.21) * mm, "mid": v(-4.74, 4.4) * mm, "end": v(-12.23, 1.21) * mm});
            skArc(sketch, "E392", {"start": v(-12.81, 3.6) * mm, "mid": v(-12.54, 2.4) * mm, "end": v(-12.23, 1.21) * mm});
            skArc(sketch, "E393", {"start": v(-12.81, 3.6) * mm, "mid": v(-10.12, 8.37) * mm, "end": v(-13.4, 12.76) * mm});
            skArc(sketch, "E394", {"start": v(-13.4, 12.76) * mm, "mid": v(-15.08, 13.11) * mm, "end": v(-16.76, 12.76) * mm});
            skArc(sketch, "E395", {"start": v(-16.76, 12.76) * mm, "mid": v(-17.81, 19.87) * mm, "end": v(-22.6, 25.23) * mm});
            skArc(sketch, "E396", {"start": v(-22.6, 25.23) * mm, "mid": v(-35.47, 28.66) * mm, "end": v(-48.35, 25.23) * mm});
            skArc(sketch, "E397", {"start": v(-48.35, 25.23) * mm, "mid": v(-53.44, 21.45) * mm, "end": v(-56.97, 16.18) * mm});
            skArc(sketch, "E398", {"start": v(-56.97, 16.18) * mm, "mid": v(-57.96, 10.18) * mm, "end": v(-55.64, 4.55) * mm});
            skArc(sketch, "E399", {"start": v(-55.64, 4.55) * mm, "mid": v(-51.79, 2.15) * mm, "end": v(-47.26, 1.85) * mm});
            skLineSegment(sketch, "E400", {"start": v(-47.26, 1.85) * mm, "end": v(-52.24, -11.64) * mm});
            skArc(sketch, "E401", {"start": v(-56.46, -16.23) * mm, "mid": v(-53.9, -14.35) * mm, "end": v(-52.24, -11.64) * mm});
            skSolve(sketch);
        }
        {
            var Q0;
            {var subQ0=sQuery(id+"F6.wireOp",EDGE,"E397");Q0=makeQuery(id+"F6.imprint","IMPRINT",FACE,{"disambiguationData":[TD([[makeQuery(id+"F6.imprint","IMPRINT",EDGE,{"derivedFrom":subQ0}),1.0]])]});}
            var Q1;
            {var subQ1=sQuery(id+"F6.wireOp",EDGE,"E371");Q1=makeQuery(id+"F6.imprint","IMPRINT",FACE,{"disambiguationData":[TD([[makeQuery(id+"F6.imprint","IMPRINT",EDGE,{"derivedFrom":subQ1}),1.0]])]});}
            var Q2;
            {var subQ4=sQuery(id+"F6.wireOp",EDGE,"E384");Q2=makeQuery(id+"F6.imprint","IMPRINT",FACE,{"disambiguationData":[TD([[makeQuery(id+"F6.imprint","IMPRINT",EDGE,{"derivedFrom":subQ4}),1.0]])]});}
            var Q3;
            {var subQ0=sQuery(id+"F6.wireOp",EDGE,"E379");Q3=makeQuery(id+"F6.imprint","IMPRINT",FACE,{"disambiguationData":[TD([[makeQuery(id+"F6.imprint","IMPRINT",EDGE,{"derivedFrom":subQ0}),1.0]])]});}
            var Q4;
            {var subQ4=sQuery(id+"F6.wireOp",EDGE,"E376");Q4=makeQuery(id+"F6.imprint","IMPRINT",FACE,{"disambiguationData":[TD([[makeQuery(id+"F6.imprint","IMPRINT",EDGE,{"derivedFrom":subQ4}),1.0]])]});}
            extrude(context, id + "F7", {"entities" : qUnion([Q0, Q1, Q2, Q3, Q4]), "operationType" : NewBodyOperationType.ADD, "depth" : 1.59 * mm, "hasSecondDirection" : true, "secondDirectionOppositeDirection" : true, "secondDirectionDepth" : 3.17 * mm});
        }
        {
            var Q0;
            Q0=makeQuery(id+"F7.opExtrude","CAP_FACE",FACE,{"disambiguationData":[OSD([sQuery(id+"F6.wireOp",EDGE,"E370"),sQuery(id+"F6.wireOp",EDGE,"E371"),sQuery(id+"F6.wireOp",EDGE,"E372"),sQuery(id+"F6.wireOp",EDGE,"E373"),sQuery(id+"F6.wireOp",EDGE,"E374"),sQuery(id+"F6.wireOp",EDGE,"E375"),sQuery(id+"F6.wireOp",EDGE,"E376"),sQuery(id+"F6.wireOp",EDGE,"E377"),sQuery(id+"F6.wireOp",EDGE,"E378"),sQuery(id+"F6.wireOp",EDGE,"E379"),sQuery(id+"F6.wireOp",EDGE,"E380"),sQuery(id+"F6.wireOp",EDGE,"E381"),sQuery(id+"F6.wireOp",EDGE,"E382"),sQuery(id+"F6.wireOp",EDGE,"E383"),sQuery(id+"F6.wireOp",EDGE,"E384"),sQuery(id+"F6.wireOp",EDGE,"E385"),sQuery(id+"F6.wireOp",EDGE,"E386"),sQuery(id+"F6.wireOp",EDGE,"E387"),sQuery(id+"F6.wireOp",EDGE,"E388"),sQuery(id+"F6.wireOp",EDGE,"E389"),sQuery(id+"F6.wireOp",EDGE,"E390"),sQuery(id+"F6.wireOp",EDGE,"E391"),sQuery(id+"F6.wireOp",EDGE,"E392"),sQuery(id+"F6.wireOp",EDGE,"E393"),sQuery(id+"F6.wireOp",EDGE,"E394"),sQuery(id+"F6.wireOp",EDGE,"E395"),sQuery(id+"F6.wireOp",EDGE,"E396"),sQuery(id+"F6.wireOp",EDGE,"E397"),sQuery(id+"F6.wireOp",EDGE,"E398"),sQuery(id+"F6.wireOp",EDGE,"E399"),sQuery(id+"F6.wireOp",EDGE,"E400"),sQuery(id+"F6.wireOp",EDGE,"E401")])],"isStart":false});
            var sketch = newSketch(context, id + "F8", { "sketchPlane" : qUnion([Q0])});
            skArc(sketch, "E402", {"start": v(-41.5, 20.2) * mm, "mid": v(-45.81, 16.98) * mm, "end": v(-48.05, 12.1) * mm});
            skArc(sketch, "E403", {"start": v(-41.5, 20.2) * mm, "mid": v(-44.22, 14.56) * mm, "end": v(-45.98, 8.57) * mm});
            skArc(sketch, "E404", {"start": v(-48.05, 12.1) * mm, "mid": v(-48.06, 10.87) * mm, "end": v(-47.72, 9.7) * mm});
            skArc(sketch, "E405", {"start": v(-47.72, 9.7) * mm, "mid": v(-46.98, 8.92) * mm, "end": v(-45.98, 8.57) * mm});
            skArc(sketch, "E406", {"start": v(-26.94, 14.27) * mm, "mid": v(-28.06, 17.97) * mm, "end": v(-31.1, 20.37) * mm});
            skArc(sketch, "E407", {"start": v(-30.15, 5.69) * mm, "mid": v(-27.6, 9.63) * mm, "end": v(-26.94, 14.27) * mm});
            skArc(sketch, "E408", {"start": v(-36.54, 2.95) * mm, "mid": v(-33.14, 3.84) * mm, "end": v(-30.15, 5.69) * mm});
            skArc(sketch, "E409", {"start": v(-31.38, 17.84) * mm, "mid": v(-31.08, 19.09) * mm, "end": v(-31.1, 20.37) * mm});
            skLineSegment(sketch, "E410", {"start": v(-36.54, 2.95) * mm, "end": v(-31.38, 17.84) * mm});
            skArc(sketch, "E411", {"start": v(-44, -15.03) * mm, "mid": v(-40.94, -9.82) * mm, "end": v(-39.33, -4.01) * mm});
            skArc(sketch, "E412", {"start": v(-39.33, -4.01) * mm, "mid": v(-31.85, -4.84) * mm, "end": v(-25.04, -1.67) * mm});
            skArc(sketch, "E413", {"start": v(-23.84, -4.01) * mm, "mid": v(-24.1, -2.67) * mm, "end": v(-25.04, -1.67) * mm});
            skArc(sketch, "E414", {"start": v(-23.84, -4.01) * mm, "mid": v(-25.89, -7.45) * mm, "end": v(-26.64, -11.39) * mm});
            skArc(sketch, "E415", {"start": v(-26.64, -11.39) * mm, "mid": v(-26.58, -13.24) * mm, "end": v(-26.12, -15.03) * mm});
            skLineSegment(sketch, "E416", {"start": v(-44, -15.03) * mm, "end": v(-26.12, -15.03) * mm});
            skArc(sketch, "E417", {"start": v(-7.64, -6.65) * mm, "mid": v(-5.37, -8.62) * mm, "end": v(-2.37, -8.63) * mm});
            skArc(sketch, "E418", {"start": v(-7.64, -6.65) * mm, "mid": v(-8, -8.82) * mm, "end": v(-6.27, -10.18) * mm});
            skArc(sketch, "E419", {"start": v(-6.27, -10.18) * mm, "mid": v(-4.17, -9.8) * mm, "end": v(-2.37, -8.63) * mm});
            skArc(sketch, "E420", {"start": v(-52.34, 4.28) * mm, "mid": v(-49.02, 3.68) * mm, "end": v(-45.73, 4.4) * mm});
            skArc(sketch, "E421", {"start": v(-56.15, 11.18) * mm, "mid": v(-55.23, 7.19) * mm, "end": v(-52.34, 4.28) * mm});
            skArc(sketch, "E422", {"start": v(-52.2, 20.17) * mm, "mid": v(-54.92, 16) * mm, "end": v(-56.15, 11.18) * mm});
            skArc(sketch, "E423", {"start": v(-32.75, 27.02) * mm, "mid": v(-43.2, 25.66) * mm, "end": v(-52.2, 20.17) * mm});
            skArc(sketch, "E424", {"start": v(-20.3, 21.02) * mm, "mid": v(-26, 25.1) * mm, "end": v(-32.75, 27.02) * mm});
            skArc(sketch, "E425", {"start": v(-19.81, 7.7) * mm, "mid": v(-18.22, 14.43) * mm, "end": v(-20.3, 21.02) * mm});
            skArc(sketch, "E426", {"start": v(-32.75, -2.82) * mm, "mid": v(-25.19, 1.1) * mm, "end": v(-19.81, 7.7) * mm});
            skArc(sketch, "E427", {"start": v(-39.6, -1.18) * mm, "mid": v(-36.33, -2.64) * mm, "end": v(-32.75, -2.82) * mm});
            skArc(sketch, "E428", {"start": v(-38.66, 0.46) * mm, "mid": v(-39.58, -0.1) * mm, "end": v(-39.6, -1.18) * mm});
            skArc(sketch, "E429", {"start": v(-38.66, 0.46) * mm, "mid": v(-32.87, 1.21) * mm, "end": v(-28.19, 4.7) * mm});
            skArc(sketch, "E430", {"start": v(-28.19, 4.7) * mm, "mid": v(-25.42, 10.02) * mm, "end": v(-24.53, 15.94) * mm});
            skArc(sketch, "E431", {"start": v(-24.53, 15.94) * mm, "mid": v(-27.1, 20.72) * mm, "end": v(-31.76, 23.5) * mm});
            skArc(sketch, "E432", {"start": v(-31.76, 23.5) * mm, "mid": v(-36.81, 24) * mm, "end": v(-41.74, 22.76) * mm});
            skArc(sketch, "E433", {"start": v(-41.74, 22.76) * mm, "mid": v(-46, 19.5) * mm, "end": v(-49.05, 15.08) * mm});
            skArc(sketch, "E434", {"start": v(-49.05, 15.08) * mm, "mid": v(-49.8, 11.63) * mm, "end": v(-49.05, 8.18) * mm});
            skArc(sketch, "E435", {"start": v(-49.05, 8.18) * mm, "mid": v(-47.54, 6.78) * mm, "end": v(-45.6, 6.13) * mm});
            skArc(sketch, "E436", {"start": v(-45.73, 4.4) * mm, "mid": v(-45.04, 5.22) * mm, "end": v(-45.6, 6.13) * mm});
            skArc(sketch, "E437", {"start": v(-34.3, 21.17) * mm, "mid": v(-36.95, 20.8) * mm, "end": v(-38.95, 19) * mm});
            skArc(sketch, "E438", {"start": v(-34.3, 17.86) * mm, "mid": v(-33.98, 19.52) * mm, "end": v(-34.3, 21.17) * mm});
            skLineSegment(sketch, "E439", {"start": v(-38.95, 19) * mm, "end": v(-49.76, -10.54) * mm});
            skLineSegment(sketch, "E440", {"start": v(-34.3, 17.86) * mm, "end": v(-43.81, -10.39) * mm});
            skArc(sketch, "E441", {"start": v(-48.7, -17.1) * mm, "mid": v(-45.74, -14.12) * mm, "end": v(-43.81, -10.39) * mm});
            skArc(sketch, "E442", {"start": v(-55.48, -17.68) * mm, "mid": v(-52.04, -14.58) * mm, "end": v(-49.76, -10.54) * mm});
            skArc(sketch, "E443", {"start": v(-55.48, -17.68) * mm, "mid": v(-63.43, -19.52) * mm, "end": v(-70.06, -24.29) * mm});
            skArc(sketch, "E444", {"start": v(-58.95, -23.37) * mm, "mid": v(-63.77, -23.92) * mm, "end": v(-68.25, -25.79) * mm});
            skArc(sketch, "E445", {"start": v(-70.06, -26.27) * mm, "mid": v(-69.13, -26.11) * mm, "end": v(-68.25, -25.79) * mm});
            skArc(sketch, "E446", {"start": v(-70.06, -24.29) * mm, "mid": v(-70.42, -25.28) * mm, "end": v(-70.06, -26.27) * mm});
            skLineSegment(sketch, "E447", {"start": v(-58.95, -23.37) * mm, "end": v(46.21, -23.37) * mm});
            skLineSegment(sketch, "E448", {"start": v(-48.7, -17.1) * mm, "end": v(46.08, -19.37) * mm});
            skArc(sketch, "E449", {"start": v(46.08, -19.37) * mm, "mid": v(54.63, -17.92) * mm, "end": v(62.02, -13.38) * mm});
            skArc(sketch, "E450", {"start": v(46.21, -23.37) * mm, "mid": v(59.26, -19.87) * mm, "end": v(68.8, -10.3) * mm});
            skArc(sketch, "E451", {"start": v(62.02, -13.38) * mm, "mid": v(63.66, -11.71) * mm, "end": v(64.78, -9.67) * mm});
            skArc(sketch, "E452", {"start": v(64.78, -9.67) * mm, "mid": v(65.03, -8.8) * mm, "end": v(65.05, -7.89) * mm});
            skArc(sketch, "E453", {"start": v(65.05, -7.89) * mm, "mid": v(64.34, -7.93) * mm, "end": v(63.74, -8.32) * mm});
            skArc(sketch, "E454", {"start": v(58.9, -12.5) * mm, "mid": v(61.58, -10.71) * mm, "end": v(63.74, -8.32) * mm});
            skLineSegment(sketch, "E455", {"start": v(58.9, -12.5) * mm, "end": v(56.43, -12.5) * mm});
            skArc(sketch, "E456", {"start": v(68.8, -10.3) * mm, "mid": v(69.32, -7.9) * mm, "end": v(68.8, -5.52) * mm});
            skArc(sketch, "E457", {"start": v(64.16, -5.17) * mm, "mid": v(61.58, -7.35) * mm, "end": v(59.3, -9.84) * mm});
            skArc(sketch, "E458", {"start": v(68.8, -5.52) * mm, "mid": v(66.54, -4.55) * mm, "end": v(64.16, -5.17) * mm});
            skLineSegment(sketch, "E459", {"start": v(59.3, -9.84) * mm, "end": v(57.72, -9.84) * mm});
            skArc(sketch, "E460", {"start": v(52.04, -15.38) * mm, "mid": v(54.63, -14.54) * mm, "end": v(56.43, -12.5) * mm});
            skLineSegment(sketch, "E461", {"start": v(52.04, -15.38) * mm, "end": v(48.83, -15.38) * mm});
            skArc(sketch, "E462", {"start": v(45.7, -13) * mm, "mid": v(46.86, -14.72) * mm, "end": v(48.83, -15.38) * mm});
            skArc(sketch, "E463", {"start": v(48.17, -10.1) * mm, "mid": v(46.42, -11.1) * mm, "end": v(45.7, -13) * mm});
            skLineSegment(sketch, "E464", {"start": v(48.17, -10.1) * mm, "end": v(53.73, -10.1) * mm});
            skArc(sketch, "E465", {"start": v(53.73, -10.1) * mm, "mid": v(52.85, -7.22) * mm, "end": v(50.61, -5.22) * mm});
            skArc(sketch, "E466", {"start": v(47.02, -9.66) * mm, "mid": v(48.9, -7.51) * mm, "end": v(50.61, -5.22) * mm});
            skArc(sketch, "E467", {"start": v(39.81, -15.22) * mm, "mid": v(43.76, -12.88) * mm, "end": v(47.02, -9.66) * mm});
            skArc(sketch, "E468", {"start": v(31.56, -14.52) * mm, "mid": v(35.63, -15.59) * mm, "end": v(39.81, -15.22) * mm});
            skArc(sketch, "E469", {"start": v(29.93, -12.1) * mm, "mid": v(30.5, -13.47) * mm, "end": v(31.56, -14.52) * mm});
            skArc(sketch, "E470", {"start": v(57.72, -9.84) * mm, "mid": v(56.78, -5.34) * mm, "end": v(53.6, -2.02) * mm});
            skArc(sketch, "E471", {"start": v(53.6, -2.02) * mm, "mid": v(56.24, 1.34) * mm, "end": v(56.72, 5.58) * mm});
            skArc(sketch, "E472", {"start": v(56.72, 5.58) * mm, "mid": v(55.9, 6.48) * mm, "end": v(54.71, 6.72) * mm});
            skArc(sketch, "E473", {"start": v(54.71, 6.72) * mm, "mid": v(51.56, 5.58) * mm, "end": v(49.4, 3.02) * mm});
            skArc(sketch, "E474", {"start": v(49.4, 3.02) * mm, "mid": v(48.5, -0.16) * mm, "end": v(49.4, -3.33) * mm});
            skArc(sketch, "E475", {"start": v(41.35, -11.58) * mm, "mid": v(45.84, -7.91) * mm, "end": v(49.4, -3.33) * mm});
            skArc(sketch, "E476", {"start": v(39.05, 0) * mm, "mid": v(35.62, -2.36) * mm, "end": v(33.9, -6.14) * mm});
            skArc(sketch, "E477", {"start": v(39.41, -4) * mm, "mid": v(39.95, -1.93) * mm, "end": v(39.05, 0) * mm});
            skArc(sketch, "E478", {"start": v(34.67, -9.51) * mm, "mid": v(37.22, -6.9) * mm, "end": v(39.41, -4) * mm});
            skArc(sketch, "E479", {"start": v(34.67, -9.51) * mm, "mid": v(36.38, -10.05) * mm, "end": v(38.1, -9.51) * mm});
            skArc(sketch, "E480", {"start": v(38.1, -9.51) * mm, "mid": v(40.81, -7.45) * mm, "end": v(43.13, -4.93) * mm});
            skArc(sketch, "E481", {"start": v(43.13, -4.93) * mm, "mid": v(44.12, -3.28) * mm, "end": v(44.52, -1.4) * mm});
            skArc(sketch, "E482", {"start": v(44.52, -1.4) * mm, "mid": v(43.8, 0.89) * mm, "end": v(41.78, 2.16) * mm});
            skArc(sketch, "E483", {"start": v(41.78, 2.16) * mm, "mid": v(38.65, 2.18) * mm, "end": v(35.69, 1.16) * mm});
            skArc(sketch, "E484", {"start": v(35.69, 1.16) * mm, "mid": v(31, -3.37) * mm, "end": v(29.47, -9.71) * mm});
            skArc(sketch, "E485", {"start": v(25.55, -12.54) * mm, "mid": v(27.74, -11.45) * mm, "end": v(29.47, -9.71) * mm});
            skArc(sketch, "E486", {"start": v(23.5, -8.24) * mm, "mid": v(23.87, -10.7) * mm, "end": v(25.55, -12.54) * mm});
            skArc(sketch, "E487", {"start": v(23.5, -8.24) * mm, "mid": v(31, 6) * mm, "end": v(33.69, 21.87) * mm});
            skArc(sketch, "E488", {"start": v(33.69, 21.87) * mm, "mid": v(32.55, 22.72) * mm, "end": v(31.2, 22.26) * mm});
            skArc(sketch, "E489", {"start": v(31.2, 22.26) * mm, "mid": v(22.34, 8.15) * mm, "end": v(19.29, -8.24) * mm});
            skArc(sketch, "E490", {"start": v(23.5, -15.9) * mm, "mid": v(27.12, -14.67) * mm, "end": v(29.93, -12.1) * mm});
            skArc(sketch, "E491", {"start": v(19.29, -12.1) * mm, "mid": v(20.69, -14.79) * mm, "end": v(23.5, -15.9) * mm});
            skArc(sketch, "E492", {"start": v(13.15, -15.9) * mm, "mid": v(16.58, -14.57) * mm, "end": v(19.29, -12.1) * mm});
            skArc(sketch, "E493", {"start": v(7.45, -10.37) * mm, "mid": v(8.97, -14.5) * mm, "end": v(13.15, -15.9) * mm});
            skArc(sketch, "E494", {"start": v(8.54, -8.24) * mm, "mid": v(7.66, -9.13) * mm, "end": v(7.45, -10.37) * mm});
            skArc(sketch, "E495", {"start": v(8.54, -8.24) * mm, "mid": v(10.9, -6.39) * mm, "end": v(12.8, -4.06) * mm});
            skArc(sketch, "E496", {"start": v(11.8, -3.28) * mm, "mid": v(8.74, -5.65) * mm, "end": v(6.4, -8.76) * mm});
            skArc(sketch, "E497", {"start": v(12.8, -4.06) * mm, "mid": v(12.6, -3.3) * mm, "end": v(11.8, -3.28) * mm});
            skArc(sketch, "E498", {"start": v(6.4, -8.76) * mm, "mid": v(5.44, -11.18) * mm, "end": v(4.98, -13.75) * mm});
            skArc(sketch, "E499", {"start": v(1.22, -16.04) * mm, "mid": v(3.38, -15.35) * mm, "end": v(4.98, -13.75) * mm});
            skArc(sketch, "E500", {"start": v(0.33, -15.1) * mm, "mid": v(0.58, -15.75) * mm, "end": v(1.22, -16.04) * mm});
            skArc(sketch, "E501", {"start": v(0.7, -12.17) * mm, "mid": v(0.5, -13.64) * mm, "end": v(0.33, -15.1) * mm});
            skArc(sketch, "E502", {"start": v(-7.4, -16.04) * mm, "mid": v(-2.95, -14.94) * mm, "end": v(0.7, -12.17) * mm});
            skArc(sketch, "E503", {"start": v(-14.18, -12.6) * mm, "mid": v(-11.26, -15.24) * mm, "end": v(-7.4, -16.04) * mm});
            skArc(sketch, "E504", {"start": v(-20.67, -16.04) * mm, "mid": v(-17.1, -14.92) * mm, "end": v(-14.18, -12.6) * mm});
            skArc(sketch, "E505", {"start": v(-24.49, -13.25) * mm, "mid": v(-23.06, -15.31) * mm, "end": v(-20.67, -16.04) * mm});
            skArc(sketch, "E506", {"start": v(-20.67, -2.62) * mm, "mid": v(-23.7, -7.53) * mm, "end": v(-24.49, -13.25) * mm});
            skArc(sketch, "E507", {"start": v(-22.47, -0.93) * mm, "mid": v(-21.73, -1.95) * mm, "end": v(-20.67, -2.62) * mm});
            skArc(sketch, "E508", {"start": v(-14.96, 2.19) * mm, "mid": v(-19.24, 1.9) * mm, "end": v(-22.47, -0.93) * mm});
            skArc(sketch, "E509", {"start": v(-14.96, -0.93) * mm, "mid": v(-14.6, 0.63) * mm, "end": v(-14.96, 2.19) * mm});
            skLineSegment(sketch, "E510", {"start": v(-14.96, -0.93) * mm, "end": v(-19.28, -10.72) * mm});
            skArc(sketch, "E511", {"start": v(-19.28, -10.72) * mm, "mid": v(-18.93, -12.07) * mm, "end": v(-17.54, -12.03) * mm});
            skArc(sketch, "E512", {"start": v(-17.54, -12.03) * mm, "mid": v(-16.23, -11.01) * mm, "end": v(-15.02, -9.87) * mm});
            skArc(sketch, "E513", {"start": v(-11.84, -1.46) * mm, "mid": v(-14.27, -5.35) * mm, "end": v(-15.02, -9.87) * mm});
            skArc(sketch, "E514", {"start": v(-2.97, 2.14) * mm, "mid": v(-7.85, 1.44) * mm, "end": v(-11.84, -1.46) * mm});
            skArc(sketch, "E515", {"start": v(1.02, -1.77) * mm, "mid": v(-0.24, 0.94) * mm, "end": v(-2.97, 2.14) * mm});
            skArc(sketch, "E516", {"start": v(-1.92, -6.34) * mm, "mid": v(0.07, -4.39) * mm, "end": v(1.02, -1.77) * mm});
            skArc(sketch, "E517", {"start": v(-5.91, -5.6) * mm, "mid": v(-4.04, -6.64) * mm, "end": v(-1.92, -6.34) * mm});
            skArc(sketch, "E518", {"start": v(-5.91, -3.4) * mm, "mid": v(-6.26, -4.5) * mm, "end": v(-5.91, -5.6) * mm});
            skArc(sketch, "E519", {"start": v(-5.91, -3.4) * mm, "mid": v(-4.77, -3.32) * mm, "end": v(-3.86, -2.62) * mm});
            skArc(sketch, "E520", {"start": v(-3.86, -2.62) * mm, "mid": v(-3.75, -1.29) * mm, "end": v(-4.74, -0.38) * mm});
            skArc(sketch, "E521", {"start": v(-4.74, -0.38) * mm, "mid": v(-5.51, -0.33) * mm, "end": v(-6.24, -0.61) * mm});
            skArc(sketch, "E522", {"start": v(-6.24, -0.61) * mm, "mid": v(-8.38, -2.79) * mm, "end": v(-9.82, -5.48) * mm});
            skArc(sketch, "E523", {"start": v(-9.82, -5.48) * mm, "mid": v(-10.16, -8.15) * mm, "end": v(-9.82, -10.81) * mm});
            skArc(sketch, "E524", {"start": v(-9.82, -10.81) * mm, "mid": v(-9.15, -11.71) * mm, "end": v(-8.13, -12.19) * mm});
            skArc(sketch, "E525", {"start": v(-8.13, -12.19) * mm, "mid": v(-6.01, -12.39) * mm, "end": v(-3.89, -12.19) * mm});
            skArc(sketch, "E526", {"start": v(-3.89, -12.19) * mm, "mid": v(-0.82, -10.56) * mm, "end": v(1.7, -8.17) * mm});
            skArc(sketch, "E527", {"start": v(1.7, -8.17) * mm, "mid": v(3.4, -3.58) * mm, "end": v(4.76, 1.11) * mm});
            skArc(sketch, "E528", {"start": v(15.24, 22.44) * mm, "mid": v(8.16, 12.68) * mm, "end": v(4.76, 1.11) * mm});
            skArc(sketch, "E529", {"start": v(17.94, 21.65) * mm, "mid": v(16.83, 22.85) * mm, "end": v(15.24, 22.44) * mm});
            skArc(sketch, "E530", {"start": v(7.32, -3.9) * mm, "mid": v(15.13, 7.83) * mm, "end": v(17.94, 21.65) * mm});
            skArc(sketch, "E531", {"start": v(7.32, -3.9) * mm, "mid": v(7.4, -4.36) * mm, "end": v(7.82, -4.18) * mm});
            skArc(sketch, "E532", {"start": v(14.8, 1.73) * mm, "mid": v(10.92, -0.76) * mm, "end": v(7.82, -4.18) * mm});
            skArc(sketch, "E533", {"start": v(18.73, 1.11) * mm, "mid": v(16.85, 1.95) * mm, "end": v(14.8, 1.73) * mm});
            skArc(sketch, "E534", {"start": v(18.52, -2.71) * mm, "mid": v(19.3, -0.83) * mm, "end": v(18.73, 1.11) * mm});
            skArc(sketch, "E535", {"start": v(12.09, -9) * mm, "mid": v(15.5, -6.06) * mm, "end": v(18.52, -2.71) * mm});
            skArc(sketch, "E536", {"start": v(12.09, -9) * mm, "mid": v(12.15, -10.76) * mm, "end": v(13.15, -12.19) * mm});
            skArc(sketch, "E537", {"start": v(13.15, -12.19) * mm, "mid": v(14.2, -12.43) * mm, "end": v(15.26, -12.19) * mm});
            skArc(sketch, "E538", {"start": v(15.26, -12.19) * mm, "mid": v(17.5, -10.44) * mm, "end": v(19.29, -8.24) * mm});
            skArc(sketch, "E539", {"start": v(33.9, -6.14) * mm, "mid": v(33.69, -8.34) * mm, "end": v(33.9, -10.54) * mm});
            skArc(sketch, "E540", {"start": v(33.9, -10.54) * mm, "mid": v(35, -12) * mm, "end": v(36.77, -12.45) * mm});
            skArc(sketch, "E541", {"start": v(36.77, -12.45) * mm, "mid": v(39.12, -12.32) * mm, "end": v(41.35, -11.58) * mm});
            skArc(sketch, "E542", {"start": v(49.47, -11.8) * mm, "mid": v(48.8, -12.56) * mm, "end": v(49.4, -13.38) * mm});
            skArc(sketch, "E543", {"start": v(49.4, -13.38) * mm, "mid": v(50.81, -13.5) * mm, "end": v(52.16, -13.05) * mm});
            skArc(sketch, "E544", {"start": v(52.16, -13.05) * mm, "mid": v(52.35, -12.47) * mm, "end": v(51.91, -12.04) * mm});
            skArc(sketch, "E545", {"start": v(51.91, -12.04) * mm, "mid": v(50.7, -11.77) * mm, "end": v(49.47, -11.8) * mm});
            skArc(sketch, "E546", {"start": v(53.82, 4.05) * mm, "mid": v(52.64, 3.83) * mm, "end": v(51.91, 2.88) * mm});
            skArc(sketch, "E547", {"start": v(51.91, 2.88) * mm, "mid": v(51.87, 1.58) * mm, "end": v(52.32, 0.35) * mm});
            skArc(sketch, "E548", {"start": v(54.24, 2.95) * mm, "mid": v(54.22, 3.57) * mm, "end": v(53.82, 4.05) * mm});
            skArc(sketch, "E549", {"start": v(52.32, 0.35) * mm, "mid": v(53.37, 1.59) * mm, "end": v(54.24, 2.95) * mm});
            skArc(sketch, "E550", {"start": v(29.06, 16.05) * mm, "mid": v(25.52, 6.56) * mm, "end": v(23.91, -3.44) * mm});
            skArc(sketch, "E551", {"start": v(23.91, -3.44) * mm, "mid": v(27.75, 5.97) * mm, "end": v(29.06, 16.05) * mm});
            skArc(sketch, "E552", {"start": v(13.12, 15.78) * mm, "mid": v(10.03, 9.09) * mm, "end": v(8.46, 1.89) * mm});
            skArc(sketch, "E553", {"start": v(8.46, 1.89) * mm, "mid": v(12.06, 8.4) * mm, "end": v(13.12, 15.78) * mm});
            skArc(sketch, "E554", {"start": v(-12.99, 10.04) * mm, "mid": v(-16.04, 10.8) * mm, "end": v(-18.3, 8.63) * mm});
            skArc(sketch, "E555", {"start": v(-18.3, 8.63) * mm, "mid": v(-17.84, 6.21) * mm, "end": v(-15.53, 5.38) * mm});
            skArc(sketch, "E556", {"start": v(-15.53, 5.38) * mm, "mid": v(-13.82, 5.95) * mm, "end": v(-12.77, 7.4) * mm});
            skArc(sketch, "E557", {"start": v(-12.77, 7.4) * mm, "mid": v(-12.52, 8.76) * mm, "end": v(-12.99, 10.04) * mm});
            skSolve(sketch);
        }
        {
            var Q0;
            Q0=makeQuery(id+"F8.imprint","IMPRINT",FACE,{"disambiguationData":[TD([[makeQuery(id+"F8.imprint","IMPRINT",EDGE,{"derivedFrom":sQuery(id+"F8.wireOp",EDGE,"E437")}),1.0]])]});
            var Q1;
            Q1=makeQuery(id+"F8.imprint","IMPRINT",FACE,{"disambiguationData":[TD([[makeQuery(id+"F8.imprint","IMPRINT",EDGE,{"derivedFrom":sQuery(id+"F8.wireOp",EDGE,"E420")}),1.0]])]});
            var Q2;
            Q2=makeQuery(id+"F8.imprint","IMPRINT",FACE,{"disambiguationData":[TD([[makeQuery(id+"F8.imprint","IMPRINT",EDGE,{"derivedFrom":sQuery(id+"F8.wireOp",EDGE,"E554")}),1.0]])]});
            extrude(context, id + "F9", {"entities" : qUnion([Q0, Q1, Q2]), "operationType" : NewBodyOperationType.ADD, "depth" : 1.59 * mm});
        }
        {
            var Q0;
            {var subQ0=sQuery(id+"F0.wireOp",EDGE,"E0");var subQ1=makeQuery(id+"F1.opExtrude","SWEPT_FACE",FACE,{"disambiguationData":[OSD([subQ0])]});Q0=makeQuery(id+"F7.boolean.opBoolean","SPLIT",FACE,{"disambiguationData":[TD([makeQuery(id+"F7.opExtrude","SWEPT_FACE",FACE,{"disambiguationData":[OSD([sQuery(id+"F6.wireOp",EDGE,"E370")])]})])],"derivedFrom":makeQuery(id+"F3.boolean.opBoolean","SPLIT",FACE,{"disambiguationData":[TD([subQ1])],"derivedFrom":makeQuery(id+"F1.opExtrude","CAP_FACE",FACE,{"disambiguationData":[OSD([subQ0,sQuery(id+"F0.wireOp",EDGE,"E1")])],"isStart":false})})});}
            var sketch = newSketch(context, id + "F10", { "sketchPlane" : qUnion([Q0])});
            skCircle(sketch, "E558", {"center": v(0, 65.33) * mm, "radius": 1.58 * mm});
            skCircle(sketch, "E559", {"center": v(0, 65.33) * mm, "radius": 2.37 * mm});
            skSolve(sketch);
        }
        {
            var Q0;
            {var subQ0=sQuery(id+"F10.wireOp",EDGE,"E558");var subQ1=sQuery(id+"F0.wireOp",EDGE,"E0");var subQ2=makeQuery(id+"F7.boolean.opBoolean","SPLIT",EDGE,{"disambiguationData":[TD([makeQuery(id+"F7.opExtrude","SWEPT_FACE",FACE,{"disambiguationData":[OSD([sQuery(id+"F6.wireOp",EDGE,"E370")])]})])],"derivedFrom":makeQuery(id+"F1.opExtrude","CAP_EDGE",EDGE,{"disambiguationData":[OSD([subQ1])],"isStart":false})});var subQ3=makeQuery(id+"F10.imprint","INTERSECT",VERTEX,{"disambiguationData":[OD(0.0)],"derivedFrom":[subQ2,subQ0]});Q0=makeQuery(id+"F10.imprint","IMPRINT",FACE,{"disambiguationData":[TD([[makeQuery(id+"F10.imprint","IMPRINT",EDGE,{"disambiguationData":[TD([[subQ3,-1.0]])],"derivedFrom":subQ0}),-1.0]])]});}
            var Q1;
            {var subQ0=sQuery(id+"F10.wireOp",EDGE,"E558");var subQ1=sQuery(id+"F0.wireOp",EDGE,"E0");var subQ2=makeQuery(id+"F7.boolean.opBoolean","SPLIT",EDGE,{"disambiguationData":[TD([makeQuery(id+"F7.opExtrude","SWEPT_FACE",FACE,{"disambiguationData":[OSD([sQuery(id+"F6.wireOp",EDGE,"E370")])]})])],"derivedFrom":makeQuery(id+"F1.opExtrude","CAP_EDGE",EDGE,{"disambiguationData":[OSD([subQ1])],"isStart":false})});var subQ3=makeQuery(id+"F10.imprint","INTERSECT",VERTEX,{"disambiguationData":[OD(0.0)],"derivedFrom":[subQ2,subQ0]});Q1=makeQuery(id+"F10.imprint","IMPRINT",FACE,{"disambiguationData":[TD([[makeQuery(id+"F10.imprint","IMPRINT",EDGE,{"disambiguationData":[TD([[subQ3,1.0]])],"derivedFrom":subQ0}),-1.0]])]});}
            extrude(context, id + "F11", {"entities" : qUnion([Q0, Q1]), "operationType" : NewBodyOperationType.ADD, "depth" : 0.79 * mm, "hasSecondDirection" : true, "secondDirectionOppositeDirection" : true, "secondDirectionDepth" : 1.59 * mm});
        }
        {
            var Q0;
            {var subQ0=sQuery(id+"F10.wireOp",EDGE,"E558");var subQ1=sQuery(id+"F0.wireOp",EDGE,"E0");var subQ2=makeQuery(id+"F7.boolean.opBoolean","SPLIT",EDGE,{"disambiguationData":[TD([makeQuery(id+"F7.opExtrude","SWEPT_FACE",FACE,{"disambiguationData":[OSD([sQuery(id+"F6.wireOp",EDGE,"E370")])]})])],"derivedFrom":makeQuery(id+"F1.opExtrude","CAP_EDGE",EDGE,{"disambiguationData":[OSD([subQ1])],"isStart":false})});var subQ3=makeQuery(id+"F10.imprint","INTERSECT",VERTEX,{"disambiguationData":[OD(0.0)],"derivedFrom":[subQ2,subQ0]});Q0=makeQuery(id+"F10.imprint","IMPRINT",FACE,{"disambiguationData":[TD([[makeQuery(id+"F10.imprint","IMPRINT",EDGE,{"disambiguationData":[TD([[subQ3,1.0]])],"derivedFrom":subQ0}),1.0]])]});}
            extrude(context, id + "F12", {"entities" : qUnion([Q0]), "operationType" : NewBodyOperationType.REMOVE, "oppositeDirection" : true, "depth" : 25.4 * mm});
        }
    });
